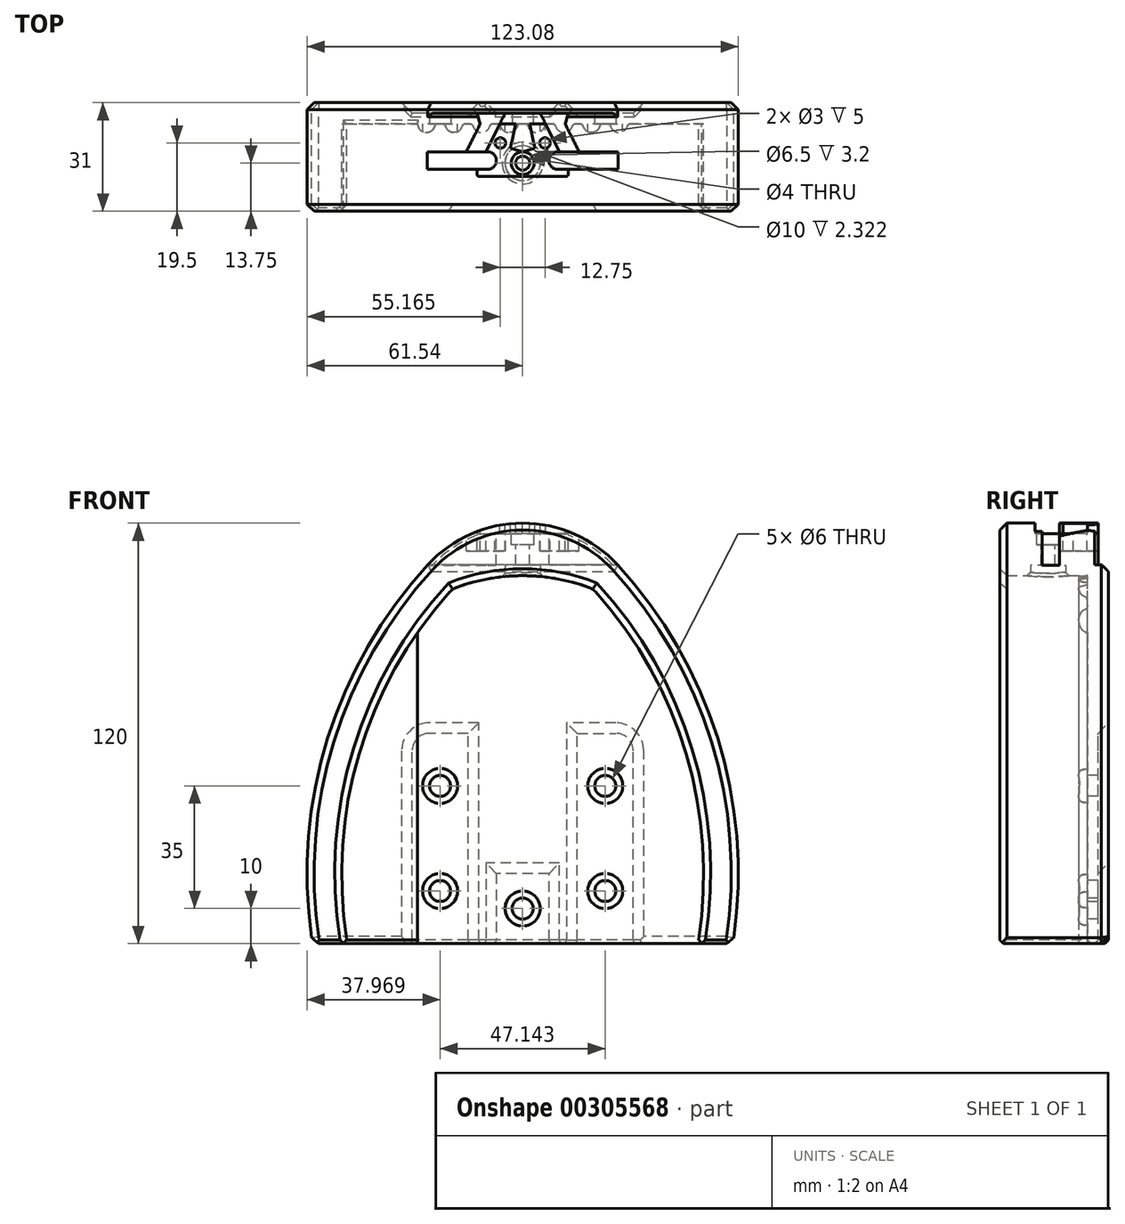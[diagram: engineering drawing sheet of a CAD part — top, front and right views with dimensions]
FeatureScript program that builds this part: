
annotation { "Feature Type Name" : "Feature", "Feature Type Description" : "" }
export const myFeature = defineFeature(function(context is Context, id is Id, definition is map)
    precondition{}
    {
        {
            assignVariable(context, id + "F0", {"name" : "LHeel", "anyValue" : 120 * mm});
        }
        {
            assignVariable(context, id + "F1", {"name" : "THeel", "anyValue" : 15 * mm});
        }
        {
            var Q0;
            Q0=qCreatedBy(makeId("Front.planeOp"),FACE);
            var sketch = newSketch(context, id + "F2", { "sketchPlane" : qUnion([Q0])});
            skArc(sketch, "E0", {"start": v(0, 120) * mm, "mid": v(-14.77, 116.9) * mm, "end": v(-27.05, 108.16) * mm});
            skArc(sketch, "E1", {"start": v(-27.05, 108.16) * mm, "mid": v(-55.9, 57.85) * mm, "end": v(-60, 0) * mm});
            skLineSegment(sketch, "E2", {"start": v(-60, 0) * mm, "end": v(0, 0) * mm});
            skArc(sketch, "E3.MirrorCS", {"start": v(0, 120) * mm, "mid": v(14.77, 116.9) * mm, "end": v(27.05, 108.16) * mm});
            skArc(sketch, "E4.MirrorCS", {"start": v(27.05, 108.16) * mm, "mid": v(55.9, 57.85) * mm, "end": v(60, 0) * mm});
            skLineSegment(sketch, "E5.MirrorCS", {"start": v(60, 0) * mm, "end": v(0, 0) * mm});
            skSolve(sketch);
        }
        {
            var Q0;
            Q0=makeQuery(id+"F2.imprint","IMPRINT",FACE,{"disambiguationData":[TD([[makeQuery(id+"F2.imprint","IMPRINT",EDGE,{"derivedFrom":sQuery(id+"F2.wireOp",EDGE,"E0")}),1.0]])]});
            extrude(context, id + "F3", {"entities" : qUnion([Q0]), "depth" : 3 * mm});
        }
        {
            var Q0;
            Q0=makeQuery(id+"F3.opExtrude","CAP_FACE",FACE,{"disambiguationData":[OSD([sQuery(id+"F2.wireOp",EDGE,"E0"),sQuery(id+"F2.wireOp",EDGE,"E1"),sQuery(id+"F2.wireOp",EDGE,"E2"),sQuery(id+"F2.wireOp",EDGE,"E3.MirrorCS"),sQuery(id+"F2.wireOp",EDGE,"E4.MirrorCS"),sQuery(id+"F2.wireOp",EDGE,"E5.MirrorCS")])],"isStart":false});
            var sketch = newSketch(context, id + "F4", { "sketchPlane" : qUnion([Q0])});
            skArc(sketch, "E6", {"start": v(0, 120) * mm, "mid": v(-14.77, 116.9) * mm, "end": v(-27.05, 108.16) * mm});
            skArc(sketch, "E7", {"start": v(-27.05, 108.16) * mm, "mid": v(-55.9, 57.85) * mm, "end": v(-60, 0) * mm});
            skArc(sketch, "E8", {"start": v(-20.01, 101.23) * mm, "mid": v(-46.72, 54.09) * mm, "end": v(-50, 0) * mm});
            skLineSegment(sketch, "E9", {"start": v(-60, 0) * mm, "end": v(-50, 0) * mm});
            skArc(sketch, "E10.MirrorCS", {"start": v(20.01, 101.23) * mm, "mid": v(46.72, 54.09) * mm, "end": v(50, 0) * mm});
            skLineSegment(sketch, "E11.MirrorCS", {"start": v(60, 0) * mm, "end": v(50, 0) * mm});
            skArc(sketch, "E12.MirrorCS", {"start": v(27.05, 108.16) * mm, "mid": v(55.9, 57.85) * mm, "end": v(60, 0) * mm});
            skArc(sketch, "E13.MirrorCS", {"start": v(0, 120) * mm, "mid": v(14.77, 116.9) * mm, "end": v(27.05, 108.16) * mm});
            skArc(sketch, "E14", {"start": v(20.01, 101.23) * mm, "mid": v(0, 105) * mm, "end": v(-20.01, 101.23) * mm});
            skPoint(sketch, "E15", {"position": v(0, 105) * mm});
            skSolve(sketch);
        }
        {
            var Q0;
            Q0=qSketchRegion(id+"F4",true);
            extrude(context, id + "F5", {"entities" : qUnion([Q0]), "operationType" : NewBodyOperationType.ADD, "depth" : 25 * mm});
        }
        {
            var Q0;
            Q0=makeQuery(id+"F3.opExtrude","SWEPT_FACE",FACE,{"disambiguationData":[OSD([sQuery(id+"F2.wireOp",EDGE,"E2"),sQuery(id+"F2.wireOp",EDGE,"E5.MirrorCS")])]});
            var sketch = newSketch(context, id + "F6", { "sketchPlane" : qUnion([Q0])});
            skArc(sketch, "E16", {"start": v(-25, 3) * mm, "mid": v(-27.5, 5.5) * mm, "end": v(-30, 3) * mm});
            skLineSegment(sketch, "E17", {"start": v(-30, 3) * mm, "end": v(-25, 3) * mm});
            skArc(sketch, "E18.1.0.0", {"start": v(-17.14, 3) * mm, "mid": v(-19.64, 5.5) * mm, "end": v(-22.14, 3) * mm});
            skArc(sketch, "E18.2.0.0", {"start": v(-9.29, 3) * mm, "mid": v(-11.79, 5.5) * mm, "end": v(-14.29, 3) * mm});
            skArc(sketch, "E18.3.0.0", {"start": v(-1.43, 3) * mm, "mid": v(-3.93, 5.5) * mm, "end": v(-6.43, 3) * mm});
            skArc(sketch, "E18.4.0.0", {"start": v(6.43, 3) * mm, "mid": v(3.93, 5.5) * mm, "end": v(1.43, 3) * mm});
            skArc(sketch, "E18.5.0.0", {"start": v(14.29, 3) * mm, "mid": v(11.79, 5.5) * mm, "end": v(9.29, 3) * mm});
            skArc(sketch, "E18.6.0.0", {"start": v(22.14, 3) * mm, "mid": v(19.64, 5.5) * mm, "end": v(17.14, 3) * mm});
            skArc(sketch, "E18.7.0.0", {"start": v(30, 3) * mm, "mid": v(27.5, 5.5) * mm, "end": v(25, 3) * mm});
            skLineSegment(sketch, "E18.direction1", {"start": v(-30, 3) * mm, "end": v(-22.14, 3) * mm, "construction": true});
            skSolve(sketch);
        }
        {
            var Q0;
            Q0=qSketchRegion(id+"F6",true);
            var Q1;
            {var subQ0=sQuery(id+"F6.wireOp",EDGE,"E18.1.0.0");Q1=makeQuery(id+"F6.imprint","IMPRINT",FACE,{"disambiguationData":[TD([[makeQuery(id+"F6.imprint","IMPRINT",EDGE,{"derivedFrom":subQ0}),1.0]])]});}
            var Q2;
            {var subQ0=sQuery(id+"F6.wireOp",EDGE,"E18.2.0.0");Q2=makeQuery(id+"F6.imprint","IMPRINT",FACE,{"disambiguationData":[TD([[makeQuery(id+"F6.imprint","IMPRINT",EDGE,{"derivedFrom":subQ0}),1.0]])]});}
            var Q3;
            {var subQ0=sQuery(id+"F6.wireOp",EDGE,"E18.3.0.0");Q3=makeQuery(id+"F6.imprint","IMPRINT",FACE,{"disambiguationData":[TD([[makeQuery(id+"F6.imprint","IMPRINT",EDGE,{"derivedFrom":subQ0}),1.0]])]});}
            var Q4;
            {var subQ0=sQuery(id+"F6.wireOp",EDGE,"E18.4.0.0");Q4=makeQuery(id+"F6.imprint","IMPRINT",FACE,{"disambiguationData":[TD([[makeQuery(id+"F6.imprint","IMPRINT",EDGE,{"derivedFrom":subQ0}),1.0]])]});}
            var Q5;
            {var subQ0=sQuery(id+"F6.wireOp",EDGE,"E18.5.0.0");Q5=makeQuery(id+"F6.imprint","IMPRINT",FACE,{"disambiguationData":[TD([[makeQuery(id+"F6.imprint","IMPRINT",EDGE,{"derivedFrom":subQ0}),1.0]])]});}
            var Q6;
            {var subQ0=sQuery(id+"F6.wireOp",EDGE,"E18.6.0.0");Q6=makeQuery(id+"F6.imprint","IMPRINT",FACE,{"disambiguationData":[TD([[makeQuery(id+"F6.imprint","IMPRINT",EDGE,{"derivedFrom":subQ0}),1.0]])]});}
            var Q7;
            {var subQ0=sQuery(id+"F6.wireOp",EDGE,"E18.7.0.0");Q7=makeQuery(id+"F6.imprint","IMPRINT",FACE,{"disambiguationData":[TD([[makeQuery(id+"F6.imprint","IMPRINT",EDGE,{"derivedFrom":subQ0}),1.0]])]});}
            var Q8;
            {var subQ0=sQuery(id+"F6.wireOp",EDGE,"E18.8.0.0");Q8=makeQuery(id+"F6.imprint","IMPRINT",FACE,{"disambiguationData":[TD([[makeQuery(id+"F6.imprint","IMPRINT",EDGE,{"derivedFrom":subQ0}),1.0]])]});}
            var Q9;
            {var subQ0=sQuery(id+"F6.wireOp",EDGE,"E18.9.0.0");Q9=makeQuery(id+"F6.imprint","IMPRINT",FACE,{"disambiguationData":[TD([[makeQuery(id+"F6.imprint","IMPRINT",EDGE,{"derivedFrom":subQ0}),1.0]])]});}
            extrude(context, id + "F7", {"entities" : qUnion([Q0, Q1, Q2, Q3, Q4, Q5, Q6, Q7, Q8, Q9]), "operationType" : NewBodyOperationType.ADD, "endBound" : BoundingType.UP_TO_NEXT, "oppositeDirection" : true, "depth" : 25 * mm});
        }
        {
            var Q0;
            {var subQ0=sQuery(id+"F6.wireOp",EDGE,"E17");var subQ1=sQuery(id+"F6.wireOp",EDGE,"E16");var subQ2=sQuery(id+"F2.wireOp",EDGE,"E5.MirrorCS");var subQ3=sQuery(id+"F2.wireOp",EDGE,"E2");Q0=makeQuery(id+"F7.opExtrude","SWEPT_EDGE",EDGE,{"disambiguationData":[OSD([subQ3,subQ2,subQ1,subQ0]),TDD([makeQuery(id+"F6.imprint","INTERSECT",VERTEX,{"disambiguationData":[OD(0.0)],"derivedFrom":[makeQuery(id+"F3.opExtrude","CAP_EDGE",EDGE,{"disambiguationData":[OSD([subQ3,subQ2])],"isStart":false}),subQ1,subQ0]})])]});}
            var Q1;
            {var subQ0=sQuery(id+"F6.wireOp",EDGE,"E18.1.0.0");var subQ1=sQuery(id+"F2.wireOp",EDGE,"E5.MirrorCS");var subQ2=sQuery(id+"F2.wireOp",EDGE,"E2");Q1=makeQuery(id+"F7.opExtrude","SWEPT_EDGE",EDGE,{"disambiguationData":[OSD([subQ2,subQ1,subQ0]),TDD([makeQuery(id+"F6.imprint","INTERSECT",VERTEX,{"disambiguationData":[OD(0.0)],"derivedFrom":[makeQuery(id+"F3.opExtrude","CAP_EDGE",EDGE,{"disambiguationData":[OSD([subQ2,subQ1])],"isStart":false}),subQ0]})])]});}
            var Q2;
            {var subQ0=sQuery(id+"F6.wireOp",EDGE,"E18.2.0.0");var subQ1=sQuery(id+"F2.wireOp",EDGE,"E5.MirrorCS");var subQ2=sQuery(id+"F2.wireOp",EDGE,"E2");Q2=makeQuery(id+"F7.opExtrude","SWEPT_EDGE",EDGE,{"disambiguationData":[OSD([subQ2,subQ1,subQ0]),TDD([makeQuery(id+"F6.imprint","INTERSECT",VERTEX,{"disambiguationData":[OD(0.0)],"derivedFrom":[makeQuery(id+"F3.opExtrude","CAP_EDGE",EDGE,{"disambiguationData":[OSD([subQ2,subQ1])],"isStart":false}),subQ0]})])]});}
            var Q3;
            {var subQ0=sQuery(id+"F6.wireOp",EDGE,"E18.3.0.0");var subQ1=sQuery(id+"F2.wireOp",EDGE,"E5.MirrorCS");var subQ2=sQuery(id+"F2.wireOp",EDGE,"E2");Q3=makeQuery(id+"F7.opExtrude","SWEPT_EDGE",EDGE,{"disambiguationData":[OSD([subQ2,subQ1,subQ0]),TDD([makeQuery(id+"F6.imprint","INTERSECT",VERTEX,{"disambiguationData":[OD(0.0)],"derivedFrom":[makeQuery(id+"F3.opExtrude","CAP_EDGE",EDGE,{"disambiguationData":[OSD([subQ2,subQ1])],"isStart":false}),subQ0]})])]});}
            var Q4;
            {var subQ0=sQuery(id+"F6.wireOp",EDGE,"E18.4.0.0");var subQ1=sQuery(id+"F2.wireOp",EDGE,"E5.MirrorCS");var subQ2=sQuery(id+"F2.wireOp",EDGE,"E2");Q4=makeQuery(id+"F7.opExtrude","SWEPT_EDGE",EDGE,{"disambiguationData":[OSD([subQ2,subQ1,subQ0]),TDD([makeQuery(id+"F6.imprint","INTERSECT",VERTEX,{"disambiguationData":[OD(0.0)],"derivedFrom":[makeQuery(id+"F3.opExtrude","CAP_EDGE",EDGE,{"disambiguationData":[OSD([subQ2,subQ1])],"isStart":false}),subQ0]})])]});}
            var Q5;
            {var subQ0=sQuery(id+"F6.wireOp",EDGE,"E18.5.0.0");var subQ1=sQuery(id+"F2.wireOp",EDGE,"E5.MirrorCS");var subQ2=sQuery(id+"F2.wireOp",EDGE,"E2");Q5=makeQuery(id+"F7.opExtrude","SWEPT_EDGE",EDGE,{"disambiguationData":[OSD([subQ2,subQ1,subQ0]),TDD([makeQuery(id+"F6.imprint","INTERSECT",VERTEX,{"disambiguationData":[OD(0.0)],"derivedFrom":[makeQuery(id+"F3.opExtrude","CAP_EDGE",EDGE,{"disambiguationData":[OSD([subQ2,subQ1])],"isStart":false}),subQ0]})])]});}
            var Q6;
            {var subQ0=sQuery(id+"F6.wireOp",EDGE,"E18.6.0.0");var subQ1=sQuery(id+"F2.wireOp",EDGE,"E5.MirrorCS");var subQ2=sQuery(id+"F2.wireOp",EDGE,"E2");Q6=makeQuery(id+"F7.opExtrude","SWEPT_EDGE",EDGE,{"disambiguationData":[OSD([subQ2,subQ1,subQ0]),TDD([makeQuery(id+"F6.imprint","INTERSECT",VERTEX,{"disambiguationData":[OD(0.0)],"derivedFrom":[makeQuery(id+"F3.opExtrude","CAP_EDGE",EDGE,{"disambiguationData":[OSD([subQ2,subQ1])],"isStart":false}),subQ0]})])]});}
            var Q7;
            {var subQ0=sQuery(id+"F6.wireOp",EDGE,"E18.7.0.0");var subQ1=sQuery(id+"F2.wireOp",EDGE,"E5.MirrorCS");var subQ2=sQuery(id+"F2.wireOp",EDGE,"E2");Q7=makeQuery(id+"F7.opExtrude","SWEPT_EDGE",EDGE,{"disambiguationData":[OSD([subQ2,subQ1,subQ0]),TDD([makeQuery(id+"F6.imprint","INTERSECT",VERTEX,{"disambiguationData":[OD(0.0)],"derivedFrom":[makeQuery(id+"F3.opExtrude","CAP_EDGE",EDGE,{"disambiguationData":[OSD([subQ2,subQ1])],"isStart":false}),subQ0]})])]});}
            var Q8;
            {var subQ0=sQuery(id+"F6.wireOp",EDGE,"E18.8.0.0");var subQ1=sQuery(id+"F2.wireOp",EDGE,"E5.MirrorCS");var subQ2=sQuery(id+"F2.wireOp",EDGE,"E2");Q8=makeQuery(id+"F7.opExtrude","SWEPT_EDGE",EDGE,{"disambiguationData":[OSD([subQ2,subQ1,subQ0]),TDD([makeQuery(id+"F6.imprint","INTERSECT",VERTEX,{"disambiguationData":[OD(0.0)],"derivedFrom":[makeQuery(id+"F3.opExtrude","CAP_EDGE",EDGE,{"disambiguationData":[OSD([subQ2,subQ1])],"isStart":false}),subQ0]})])]});}
            var Q9;
            {var subQ0=sQuery(id+"F6.wireOp",EDGE,"E18.9.0.0");var subQ1=sQuery(id+"F2.wireOp",EDGE,"E5.MirrorCS");var subQ2=sQuery(id+"F2.wireOp",EDGE,"E2");Q9=makeQuery(id+"F7.opExtrude","SWEPT_EDGE",EDGE,{"disambiguationData":[OSD([subQ2,subQ1,subQ0]),TDD([makeQuery(id+"F6.imprint","INTERSECT",VERTEX,{"disambiguationData":[OD(0.0)],"derivedFrom":[makeQuery(id+"F3.opExtrude","CAP_EDGE",EDGE,{"disambiguationData":[OSD([subQ2,subQ1])],"isStart":false}),subQ0]})])]});}
            var Q10;
            {var subQ0=sQuery(id+"F6.wireOp",EDGE,"E18.9.0.0");var subQ1=sQuery(id+"F2.wireOp",EDGE,"E5.MirrorCS");var subQ2=sQuery(id+"F2.wireOp",EDGE,"E2");Q10=makeQuery(id+"F7.opExtrude","SWEPT_EDGE",EDGE,{"disambiguationData":[OSD([subQ2,subQ1,subQ0]),TDD([makeQuery(id+"F6.imprint","INTERSECT",VERTEX,{"disambiguationData":[OD(1.0)],"derivedFrom":[makeQuery(id+"F3.opExtrude","CAP_EDGE",EDGE,{"disambiguationData":[OSD([subQ2,subQ1])],"isStart":false}),subQ0]})])]});}
            var Q11;
            {var subQ0=sQuery(id+"F6.wireOp",EDGE,"E18.8.0.0");var subQ1=sQuery(id+"F2.wireOp",EDGE,"E5.MirrorCS");var subQ2=sQuery(id+"F2.wireOp",EDGE,"E2");Q11=makeQuery(id+"F7.opExtrude","SWEPT_EDGE",EDGE,{"disambiguationData":[OSD([subQ2,subQ1,subQ0]),TDD([makeQuery(id+"F6.imprint","INTERSECT",VERTEX,{"disambiguationData":[OD(1.0)],"derivedFrom":[makeQuery(id+"F3.opExtrude","CAP_EDGE",EDGE,{"disambiguationData":[OSD([subQ2,subQ1])],"isStart":false}),subQ0]})])]});}
            var Q12;
            {var subQ0=sQuery(id+"F6.wireOp",EDGE,"E18.7.0.0");var subQ1=sQuery(id+"F2.wireOp",EDGE,"E5.MirrorCS");var subQ2=sQuery(id+"F2.wireOp",EDGE,"E2");Q12=makeQuery(id+"F7.opExtrude","SWEPT_EDGE",EDGE,{"disambiguationData":[OSD([subQ2,subQ1,subQ0]),TDD([makeQuery(id+"F6.imprint","INTERSECT",VERTEX,{"disambiguationData":[OD(1.0)],"derivedFrom":[makeQuery(id+"F3.opExtrude","CAP_EDGE",EDGE,{"disambiguationData":[OSD([subQ2,subQ1])],"isStart":false}),subQ0]})])]});}
            var Q13;
            {var subQ0=sQuery(id+"F6.wireOp",EDGE,"E18.6.0.0");var subQ1=sQuery(id+"F2.wireOp",EDGE,"E5.MirrorCS");var subQ2=sQuery(id+"F2.wireOp",EDGE,"E2");Q13=makeQuery(id+"F7.opExtrude","SWEPT_EDGE",EDGE,{"disambiguationData":[OSD([subQ2,subQ1,subQ0]),TDD([makeQuery(id+"F6.imprint","INTERSECT",VERTEX,{"disambiguationData":[OD(1.0)],"derivedFrom":[makeQuery(id+"F3.opExtrude","CAP_EDGE",EDGE,{"disambiguationData":[OSD([subQ2,subQ1])],"isStart":false}),subQ0]})])]});}
            var Q14;
            {var subQ0=sQuery(id+"F6.wireOp",EDGE,"E18.5.0.0");var subQ1=sQuery(id+"F2.wireOp",EDGE,"E5.MirrorCS");var subQ2=sQuery(id+"F2.wireOp",EDGE,"E2");Q14=makeQuery(id+"F7.opExtrude","SWEPT_EDGE",EDGE,{"disambiguationData":[OSD([subQ2,subQ1,subQ0]),TDD([makeQuery(id+"F6.imprint","INTERSECT",VERTEX,{"disambiguationData":[OD(1.0)],"derivedFrom":[makeQuery(id+"F3.opExtrude","CAP_EDGE",EDGE,{"disambiguationData":[OSD([subQ2,subQ1])],"isStart":false}),subQ0]})])]});}
            var Q15;
            {var subQ0=sQuery(id+"F6.wireOp",EDGE,"E18.4.0.0");var subQ1=sQuery(id+"F2.wireOp",EDGE,"E5.MirrorCS");var subQ2=sQuery(id+"F2.wireOp",EDGE,"E2");Q15=makeQuery(id+"F7.opExtrude","SWEPT_EDGE",EDGE,{"disambiguationData":[OSD([subQ2,subQ1,subQ0]),TDD([makeQuery(id+"F6.imprint","INTERSECT",VERTEX,{"disambiguationData":[OD(1.0)],"derivedFrom":[makeQuery(id+"F3.opExtrude","CAP_EDGE",EDGE,{"disambiguationData":[OSD([subQ2,subQ1])],"isStart":false}),subQ0]})])]});}
            var Q16;
            {var subQ0=sQuery(id+"F6.wireOp",EDGE,"E18.3.0.0");var subQ1=sQuery(id+"F2.wireOp",EDGE,"E5.MirrorCS");var subQ2=sQuery(id+"F2.wireOp",EDGE,"E2");Q16=makeQuery(id+"F7.opExtrude","SWEPT_EDGE",EDGE,{"disambiguationData":[OSD([subQ2,subQ1,subQ0]),TDD([makeQuery(id+"F6.imprint","INTERSECT",VERTEX,{"disambiguationData":[OD(1.0)],"derivedFrom":[makeQuery(id+"F3.opExtrude","CAP_EDGE",EDGE,{"disambiguationData":[OSD([subQ2,subQ1])],"isStart":false}),subQ0]})])]});}
            var Q17;
            {var subQ0=sQuery(id+"F6.wireOp",EDGE,"E18.2.0.0");var subQ1=sQuery(id+"F2.wireOp",EDGE,"E5.MirrorCS");var subQ2=sQuery(id+"F2.wireOp",EDGE,"E2");Q17=makeQuery(id+"F7.opExtrude","SWEPT_EDGE",EDGE,{"disambiguationData":[OSD([subQ2,subQ1,subQ0]),TDD([makeQuery(id+"F6.imprint","INTERSECT",VERTEX,{"disambiguationData":[OD(1.0)],"derivedFrom":[makeQuery(id+"F3.opExtrude","CAP_EDGE",EDGE,{"disambiguationData":[OSD([subQ2,subQ1])],"isStart":false}),subQ0]})])]});}
            var Q18;
            {var subQ0=sQuery(id+"F6.wireOp",EDGE,"E18.1.0.0");var subQ1=sQuery(id+"F2.wireOp",EDGE,"E5.MirrorCS");var subQ2=sQuery(id+"F2.wireOp",EDGE,"E2");Q18=makeQuery(id+"F7.opExtrude","SWEPT_EDGE",EDGE,{"disambiguationData":[OSD([subQ2,subQ1,subQ0]),TDD([makeQuery(id+"F6.imprint","INTERSECT",VERTEX,{"disambiguationData":[OD(1.0)],"derivedFrom":[makeQuery(id+"F3.opExtrude","CAP_EDGE",EDGE,{"disambiguationData":[OSD([subQ2,subQ1])],"isStart":false}),subQ0]})])]});}
            var Q19;
            {var subQ0=sQuery(id+"F6.wireOp",EDGE,"E17");var subQ1=sQuery(id+"F6.wireOp",EDGE,"E16");var subQ2=sQuery(id+"F2.wireOp",EDGE,"E5.MirrorCS");var subQ3=sQuery(id+"F2.wireOp",EDGE,"E2");Q19=makeQuery(id+"F7.opExtrude","SWEPT_EDGE",EDGE,{"disambiguationData":[OSD([subQ3,subQ2,subQ1,subQ0]),TDD([makeQuery(id+"F6.imprint","INTERSECT",VERTEX,{"disambiguationData":[OD(1.0)],"derivedFrom":[makeQuery(id+"F3.opExtrude","CAP_EDGE",EDGE,{"disambiguationData":[OSD([subQ3,subQ2])],"isStart":false}),subQ1,subQ0]})])]});}
            fillet(context, id + "F8", {"entities" : qUnion([Q0, Q1, Q2, Q3, Q4, Q5, Q6, Q7, Q8, Q9, Q10, Q11, Q12, Q13, Q14, Q15, Q16, Q17, Q18, Q19]), "radius" : 1 * mm, "tangentPropagation" : true, "allowEdgeOverflow" : false});
        }
        {
            var Q0;
            Q0=qCreatedBy(makeId("Top.planeOp"),FACE);
            cPlane(context, id + "F9", {"entities" : qUnion([Q0]), "cplaneType" : CPlaneType.OFFSET, "offset" : getVariable(context, 'LHeel'), "width" : 150 * mm, "height" : 150 * mm});
        }
        {
            var Q0;
            Q0=qCreatedBy(id+"F9.planeOp",FACE);
            var sketch = newSketch(context, id + "F10", { "sketchPlane" : qUnion([Q0])});
            skLineSegment(sketch, "E19", {"start": v(35, -11) * mm, "end": v(10, -11) * mm});
            skLineSegment(sketch, "E20", {"start": v(10, -16) * mm, "end": v(35, -16) * mm});
            skLineSegment(sketch, "E21", {"start": v(35, -16) * mm, "end": v(35, -11) * mm});
            skArc(sketch, "E22", {"start": v(10, -11) * mm, "mid": v(7.5, -13.5) * mm, "end": v(10, -16) * mm});
            skLineSegment(sketch, "E23.MirrorCS", {"start": v(-35, -11) * mm, "end": v(-10, -11) * mm});
            skLineSegment(sketch, "E24.MirrorCS", {"start": v(-35, -16) * mm, "end": v(-35, -11) * mm});
            skLineSegment(sketch, "E25.MirrorCS", {"start": v(-10, -16) * mm, "end": v(-35, -16) * mm});
            skArc(sketch, "E26.MirrorCS", {"start": v(-10, -11) * mm, "mid": v(-7.5, -13.5) * mm, "end": v(-10, -16) * mm});
            skSolve(sketch);
        }
        {
            var Q0;
            Q0=qSketchRegion(id+"F10",true);
            extrude(context, id + "F11", {"entities" : qUnion([Q0]), "operationType" : NewBodyOperationType.REMOVE, "oppositeDirection" : true, "depth" : 12 * mm});
        }
        {
            var Q0;
            Q0=qCreatedBy(id+"F9.planeOp",FACE);
            var sketch = newSketch(context, id + "F12", { "sketchPlane" : qUnion([Q0])});
            skLineSegment(sketch, "E27", {"start": v(-5, 0) * mm, "end": v(-10.5, -11) * mm});
            skLineSegment(sketch, "E28", {"start": v(-10.5, -11) * mm, "end": v(-16.1, -11) * mm});
            skLineSegment(sketch, "E29", {"start": v(-16.1, -11) * mm, "end": v(-12.16, -3.14) * mm});
            skLineSegment(sketch, "E30", {"start": v(-12.16, -3.14) * mm, "end": v(-13, 0) * mm});
            skLineSegment(sketch, "E31", {"start": v(-13, 0) * mm, "end": v(-5, 0) * mm});
            skLineSegment(sketch, "E32.MirrorCS", {"start": v(12.16, -3.14) * mm, "end": v(13, 0) * mm});
            skLineSegment(sketch, "E33.MirrorCS", {"start": v(13, 0) * mm, "end": v(5, 0) * mm});
            skLineSegment(sketch, "E34.MirrorCS", {"start": v(10.5, -11) * mm, "end": v(16.1, -11) * mm});
            skLineSegment(sketch, "E35.MirrorCS", {"start": v(16.1, -11) * mm, "end": v(12.16, -3.14) * mm});
            skLineSegment(sketch, "E36.MirrorCS", {"start": v(5, 0) * mm, "end": v(10.5, -11) * mm});
            skSolve(sketch);
        }
        {
            var Q0;
            Q0=qSketchRegion(id+"F12",true);
            extrude(context, id + "F13", {"entities" : qUnion([Q0]), "operationType" : NewBodyOperationType.REMOVE, "oppositeDirection" : true, "depth" : 8 * mm});
        }
        {
            var Q0;
            Q0=qCreatedBy(id+"F9.planeOp",FACE);
            var sketch = newSketch(context, id + "F14", { "sketchPlane" : qUnion([Q0])});
            skLineSegment(sketch, "E37", {"start": v(-6.5, -3) * mm, "end": v(-2, -3) * mm});
            skLineSegment(sketch, "E38", {"start": v(-2, -3) * mm, "end": v(-3.5, -10) * mm});
            skLineSegment(sketch, "E39", {"start": v(-3.5, -10) * mm, "end": v(0, -11) * mm});
            skLineSegment(sketch, "E40", {"start": v(-6.5, -3) * mm, "end": v(-10.5, -11) * mm});
            skLineSegment(sketch, "E41", {"start": v(-13, -16) * mm, "end": v(-13, -18) * mm});
            skLineSegment(sketch, "E42", {"start": v(-13, -18) * mm, "end": v(0, -18) * mm});
            skLineSegment(sketch, "E43", {"start": v(-13, -16) * mm, "end": v(-10, -16) * mm});
            skLineSegment(sketch, "E44.MirrorCS", {"start": v(6.5, -3) * mm, "end": v(2, -3) * mm});
            skLineSegment(sketch, "E45.MirrorCS", {"start": v(6.5, -3) * mm, "end": v(10.5, -11) * mm});
            skLineSegment(sketch, "E46.MirrorCS", {"start": v(3.5, -10) * mm, "end": v(0, -11) * mm});
            skLineSegment(sketch, "E47.MirrorCS", {"start": v(2, -3) * mm, "end": v(3.5, -10) * mm});
            skLineSegment(sketch, "E48.MirrorCS", {"start": v(13, -16) * mm, "end": v(13, -18) * mm});
            skLineSegment(sketch, "E49.MirrorCS", {"start": v(13, -18) * mm, "end": v(0, -18) * mm});
            skLineSegment(sketch, "E50.MirrorCS", {"start": v(13, -16) * mm, "end": v(10, -16) * mm});
            skLineSegment(sketch, "E51", {"start": v(-10.5, -11) * mm, "end": v(-10, -11) * mm});
            skArc(sketch, "E52", {"start": v(-10, -16) * mm, "mid": v(-7.5, -13.5) * mm, "end": v(-10, -11) * mm});
            skLineSegment(sketch, "E53.MirrorCS", {"start": v(10.5, -11) * mm, "end": v(10, -11) * mm});
            skArc(sketch, "E54.MirrorCS", {"start": v(10, -16) * mm, "mid": v(7.5, -13.5) * mm, "end": v(10, -11) * mm});
            skSolve(sketch);
        }
        {
            var Q0;
            Q0=qSketchRegion(id+"F14",true);
            extrude(context, id + "F15", {"entities" : qUnion([Q0]), "operationType" : NewBodyOperationType.REMOVE, "oppositeDirection" : true, "depth" : 3 * mm});
        }
        {
            var Q0;
            Q0=makeQuery(id+"F15.boolean.opBoolean","COPY",EDGE,{"derivedFrom":makeQuery(id+"F15.opExtrude","SWEPT_EDGE",EDGE,{"disambiguationData":[OSD([sQuery(id+"F14.wireOp",EDGE,"E48.MirrorCS"),sQuery(id+"F14.wireOp",EDGE,"E49.MirrorCS")])]})});
            var Q1;
            Q1=makeQuery(id+"F15.boolean.opBoolean","COPY",EDGE,{"derivedFrom":makeQuery(id+"F15.opExtrude","SWEPT_EDGE",EDGE,{"disambiguationData":[OSD([sQuery(id+"F14.wireOp",EDGE,"E41"),sQuery(id+"F14.wireOp",EDGE,"E42")])]})});
            fillet(context, id + "F16", {"entities" : qUnion([Q0, Q1]), "radius" : .5 * mm, "tangentPropagation" : true, "allowEdgeOverflow" : false});
        }
        {
            var Q0;
            Q0=makeQuery(id+"F15.boolean.opBoolean","COPY",FACE,{"derivedFrom":makeQuery(id+"F15.opExtrude","CAP_FACE",FACE,{"disambiguationData":[OSD([sQuery(id+"F14.wireOp",EDGE,"E37"),sQuery(id+"F14.wireOp",EDGE,"E38"),sQuery(id+"F14.wireOp",EDGE,"E39"),sQuery(id+"F14.wireOp",EDGE,"E40"),sQuery(id+"F14.wireOp",EDGE,"E41"),sQuery(id+"F14.wireOp",EDGE,"E42"),sQuery(id+"F14.wireOp",EDGE,"E43"),sQuery(id+"F14.wireOp",EDGE,"E44.MirrorCS"),sQuery(id+"F14.wireOp",EDGE,"E45.MirrorCS"),sQuery(id+"F14.wireOp",EDGE,"E46.MirrorCS"),sQuery(id+"F14.wireOp",EDGE,"E47.MirrorCS"),sQuery(id+"F14.wireOp",EDGE,"E48.MirrorCS"),sQuery(id+"F14.wireOp",EDGE,"E49.MirrorCS"),sQuery(id+"F14.wireOp",EDGE,"E50.MirrorCS"),sQuery(id+"F14.wireOp",EDGE,"E51"),sQuery(id+"F14.wireOp",EDGE,"E52"),sQuery(id+"F14.wireOp",EDGE,"E53.MirrorCS"),sQuery(id+"F14.wireOp",EDGE,"E54.MirrorCS")])],"isStart":false})});
            var sketch = newSketch(context, id + "F17", { "sketchPlane" : qUnion([Q0])});
            skCircle(sketch, "E55", {"center": v(0, -14.25) * mm, "radius": 3.25 * mm});
            skSolve(sketch);
        }
        {
            var Q0;
            Q0=qSketchRegion(id+"F17",true);
            extrude(context, id + "F18", {"entities" : qUnion([Q0]), "operationType" : NewBodyOperationType.REMOVE, "oppositeDirection" : true, "depth" : 3.2 * mm});
        }
        {
            var Q0;
            Q0=makeQuery(id+"F15.boolean.opBoolean","COPY",FACE,{"derivedFrom":makeQuery(id+"F15.opExtrude","CAP_FACE",FACE,{"disambiguationData":[OSD([sQuery(id+"F14.wireOp",EDGE,"E37"),sQuery(id+"F14.wireOp",EDGE,"E38"),sQuery(id+"F14.wireOp",EDGE,"E39"),sQuery(id+"F14.wireOp",EDGE,"E40"),sQuery(id+"F14.wireOp",EDGE,"E41"),sQuery(id+"F14.wireOp",EDGE,"E42"),sQuery(id+"F14.wireOp",EDGE,"E43"),sQuery(id+"F14.wireOp",EDGE,"E44.MirrorCS"),sQuery(id+"F14.wireOp",EDGE,"E45.MirrorCS"),sQuery(id+"F14.wireOp",EDGE,"E46.MirrorCS"),sQuery(id+"F14.wireOp",EDGE,"E47.MirrorCS"),sQuery(id+"F14.wireOp",EDGE,"E48.MirrorCS"),sQuery(id+"F14.wireOp",EDGE,"E49.MirrorCS"),sQuery(id+"F14.wireOp",EDGE,"E50.MirrorCS"),sQuery(id+"F14.wireOp",EDGE,"E51"),sQuery(id+"F14.wireOp",EDGE,"E52"),sQuery(id+"F14.wireOp",EDGE,"E53.MirrorCS"),sQuery(id+"F14.wireOp",EDGE,"E54.MirrorCS")])],"isStart":false})});
            var sketch = newSketch(context, id + "F19", { "sketchPlane" : qUnion([Q0])});
            skCircle(sketch, "E56", {"center": v(6.38, -8.5) * mm, "radius": 1.5 * mm});
            skCircle(sketch, "E57.MirrorC", {"center": v(-6.38, -8.5) * mm, "radius": 1.5 * mm});
            skSolve(sketch);
        }
        {
            var Q0;
            Q0=qSketchRegion(id+"F19",true);
            extrude(context, id + "F20", {"entities" : qUnion([Q0]), "operationType" : NewBodyOperationType.REMOVE, "oppositeDirection" : true, "depth" : 5 * mm});
        }
        {
            var Q0;
            Q0=makeQuery(id+"F15.boolean.opBoolean","COPY",FACE,{"derivedFrom":makeQuery(id+"F15.opExtrude","CAP_FACE",FACE,{"disambiguationData":[OSD([sQuery(id+"F14.wireOp",EDGE,"E37"),sQuery(id+"F14.wireOp",EDGE,"E38"),sQuery(id+"F14.wireOp",EDGE,"E39"),sQuery(id+"F14.wireOp",EDGE,"E40"),sQuery(id+"F14.wireOp",EDGE,"E41"),sQuery(id+"F14.wireOp",EDGE,"E42"),sQuery(id+"F14.wireOp",EDGE,"E43"),sQuery(id+"F14.wireOp",EDGE,"E44.MirrorCS"),sQuery(id+"F14.wireOp",EDGE,"E45.MirrorCS"),sQuery(id+"F14.wireOp",EDGE,"E46.MirrorCS"),sQuery(id+"F14.wireOp",EDGE,"E47.MirrorCS"),sQuery(id+"F14.wireOp",EDGE,"E48.MirrorCS"),sQuery(id+"F14.wireOp",EDGE,"E49.MirrorCS"),sQuery(id+"F14.wireOp",EDGE,"E50.MirrorCS"),sQuery(id+"F14.wireOp",EDGE,"E51"),sQuery(id+"F14.wireOp",EDGE,"E52"),sQuery(id+"F14.wireOp",EDGE,"E53.MirrorCS"),sQuery(id+"F14.wireOp",EDGE,"E54.MirrorCS")])],"isStart":false})});
            var sketch = newSketch(context, id + "F21", { "sketchPlane" : qUnion([Q0])});
            skCircle(sketch, "E58", {"center": v(0, -14.25) * mm, "radius": 2 * mm});
            skSolve(sketch);
        }
        {
            var Q0;
            Q0=qSketchRegion(id+"F21",true);
            extrude(context, id + "F22", {"entities" : qUnion([Q0]), "operationType" : NewBodyOperationType.REMOVE, "oppositeDirection" : true, "depth" : 25 * mm});
        }
        {
            var Q0;
            Q0=qCreatedBy(makeId("Top.planeOp"),FACE);
            cPlane(context, id + "F23", {"entities" : qUnion([Q0]), "cplaneType" : CPlaneType.OFFSET, "offset" : getVariable(context, 'LHeel') - getVariable(context, 'THeel'), "width" : 150 * mm, "height" : 150 * mm});
        }
        {
            var Q0;
            Q0=qCreatedBy(id+"F23.planeOp",FACE);
            var sketch = newSketch(context, id + "F24", { "sketchPlane" : qUnion([Q0])});
            skCircle(sketch, "E59", {"center": v(0, -14.25) * mm, "radius": 2 * mm});
            skCircle(sketch, "E60", {"center": v(0, -14.25) * mm, "radius": 5 * mm});
            skSolve(sketch);
        }
        {
            var Q0;
            Q0=qSketchRegion(id+"F24",true);
            extrude(context, id + "F25", {"entities" : qUnion([Q0]), "operationType" : NewBodyOperationType.REMOVE, "depth" : 3 * mm, "hasSecondDirection" : true, "secondDirectionOppositeDirection" : true, "secondDirectionDepth" : 25 * mm});
        }
        {
            var Q0;
            {var subQ0=sQuery(id+"F6.wireOp",EDGE,"E18.6.0.0");var subQ1=sQuery(id+"F2.wireOp",EDGE,"E5.MirrorCS");var subQ2=sQuery(id+"F2.wireOp",EDGE,"E2");var subQ3=makeQuery(id+"F7.opExtrude","CAP_FACE",FACE,{"disambiguationData":[OSD([subQ2,subQ1,subQ0])],"isStart":true});var subQ4=makeQuery(id+"F7.opExtrude","CAP_FACE",FACE,{"disambiguationData":[OSD([subQ2,subQ1,sQuery(id+"F6.wireOp",EDGE,"E18.4.0.0")])],"isStart":true});var subQ5=makeQuery(id+"F7.opExtrude","CAP_FACE",FACE,{"disambiguationData":[OSD([subQ2,subQ1,sQuery(id+"F6.wireOp",EDGE,"E18.3.0.0")])],"isStart":true});var subQ6=makeQuery(id+"F3.opExtrude","SWEPT_FACE",FACE,{"disambiguationData":[OSD([subQ2,subQ1])]});var subQ7=makeQuery(id+"F7.opExtrude","CAP_FACE",FACE,{"disambiguationData":[OSD([subQ2,subQ1,sQuery(id+"F6.wireOp",EDGE,"E18.2.0.0")])],"isStart":true});var subQ8=makeQuery(id+"F5.opExtrude","SWEPT_FACE",FACE,{"disambiguationData":[OSD([sQuery(id+"F4.wireOp",EDGE,"FZn0JHBI-A9Gq-jUhd-VDxp-ANsdCAXQZEyL"),sQuery(id+"F4.wireOp",EDGE,"94862bb9-d334-4f4f-86bf-2b5ff63ee9990.MirrorCS")])]});var subQ9=sQuery(id+"F6.wireOp",EDGE,"E18.7.0.0");var subQ10=makeQuery(id+"F7.opExtrude","SWEPT_FACE",FACE,{"disambiguationData":[OSD([subQ9])]});var subQ11=makeQuery(id+"F7.opExtrude","CAP_FACE",FACE,{"disambiguationData":[OSD([subQ2,subQ1,sQuery(id+"F6.wireOp",EDGE,"E18.1.0.0")])],"isStart":true});var subQ12=makeQuery(id+"F7.opExtrude","CAP_FACE",FACE,{"disambiguationData":[OSD([subQ2,subQ1,sQuery(id+"F6.wireOp",EDGE,"E18.5.0.0")])],"isStart":true});var subQ13=makeQuery(id+"F7.opExtrude","CAP_FACE",FACE,{"disambiguationData":[OSD([sQuery(id+"F6.wireOp",EDGE,"E16"),sQuery(id+"F6.wireOp",EDGE,"E17")])],"isStart":true});var subQ14=makeQuery(id+"F7.opExtrude","CAP_FACE",FACE,{"disambiguationData":[OSD([subQ2,subQ1,subQ9])],"isStart":true});var subQ15=sQuery(id+"F6.wireOp",EDGE,"E18.8.0.0");var subQ16=makeQuery(id+"F7.opExtrude","SWEPT_FACE",FACE,{"disambiguationData":[OSD([subQ15])]});var subQ17=makeQuery(id+"F7.opExtrude","CAP_FACE",FACE,{"disambiguationData":[OSD([subQ2,subQ1,subQ15])],"isStart":true});var subQ18=sQuery(id+"F6.wireOp",EDGE,"E18.9.0.0");var subQ19=makeQuery(id+"F7.opExtrude","CAP_FACE",FACE,{"disambiguationData":[OSD([subQ2,subQ1,subQ18])],"isStart":true});var subQ20=makeQuery(id+"F3.opExtrude","CAP_FACE",FACE,{"disambiguationData":[OSD([sQuery(id+"F2.wireOp",EDGE,"E0"),sQuery(id+"F2.wireOp",EDGE,"E1"),subQ2,sQuery(id+"F2.wireOp",EDGE,"E3.MirrorCS"),sQuery(id+"F2.wireOp",EDGE,"E4.MirrorCS"),subQ1])],"isStart":false});Q0=makeQuery(id+"FuolT4ABAihHTZn_1.boolean.opBoolean","MERGE",FACE,{"derivedFrom":[makeQuery(id+"F7.boolean.opBoolean","SPLIT",FACE,{"disambiguationData":[TD([subQ6,subQ8,makeQuery(id+"F5.opExtrude","SWEPT_FACE",FACE,{"disambiguationData":[OSD([sQuery(id+"F4.wireOp",EDGE,"E10.MirrorCS")])]}),subQ13,subQ11,subQ7,subQ5,subQ4,subQ12,subQ3,subQ14,subQ16,subQ17,makeQuery(id+"F7.opExtrude","SWEPT_FACE",FACE,{"disambiguationData":[OSD([subQ18])]}),subQ19])],"derivedFrom":subQ20}),makeQuery(id+"F7.boolean.opBoolean","SPLIT",FACE,{"disambiguationData":[TD([subQ6,subQ8,subQ13,subQ11,subQ7,subQ5,subQ4,subQ12,makeQuery(id+"F7.opExtrude","SWEPT_FACE",FACE,{"disambiguationData":[OSD([subQ0])]}),subQ3,subQ10,subQ14,subQ17,subQ19])],"derivedFrom":subQ20}),makeQuery(id+"F7.boolean.opBoolean","SPLIT",FACE,{"disambiguationData":[TD([subQ6,subQ8,subQ13,subQ11,subQ7,subQ5,subQ4,subQ12,subQ3,subQ10,subQ14,subQ16,subQ17,subQ19])],"derivedFrom":subQ20}),makeQuery(id+"FuolT4ABAihHTZn_1.opExtrude","SWEPT_FACE",FACE,{"disambiguationData":[OSD([sQuery(id+"FIxBE3dgotSAZQS_1.wireOp",EDGE,"DbaOr28i-rK8a-sUH4-Cgqk-jCIZV5dNe7y5.bottom")])]})]});}
            var sketch = newSketch(context, id + "F26", { "sketchPlane" : qUnion([Q0])});
            skCircle(sketch, "E61", {"center": v(-23.57, 45) * mm, "radius": 3 * mm});
            skCircle(sketch, "E62", {"center": v(-23.57, 15) * mm, "radius": 3 * mm});
            skCircle(sketch, "E63.MirrorC", {"center": v(23.57, 45) * mm, "radius": 3 * mm});
            skCircle(sketch, "E64.MirrorC", {"center": v(23.57, 15) * mm, "radius": 3 * mm});
            skPoint(sketch, "E65", {"position": v(-23.57, 0) * mm});
            skPoint(sketch, "E66", {"position": v(23.57, 0) * mm});
            skCircle(sketch, "E67", {"center": v(0, 10) * mm, "radius": 3 * mm});
            skPoint(sketch, "E68", {"position": v(0, 0) * mm});
            skSolve(sketch);
        }
        {
            var Q0;
            Q0=qSketchRegion(id+"F26",true);
            extrude(context, id + "F27", {"entities" : qUnion([Q0]), "operationType" : NewBodyOperationType.REMOVE, "oppositeDirection" : true, "depth" : 25 * mm});
        }
        {
            var Q0;
            {var subQ0=sQuery(id+"F2.wireOp",EDGE,"E5.MirrorCS");var subQ1=sQuery(id+"F2.wireOp",EDGE,"E2");var subQ2=sQuery(id+"F6.wireOp",EDGE,"E16");var subQ3=sQuery(id+"F2.wireOp",EDGE,"E1");Q0=makeQuery(id+"F7.boolean.opBoolean","SPLIT",FACE,{"disambiguationData":[TD([makeQuery(id+"F3.opExtrude","SWEPT_FACE",FACE,{"disambiguationData":[OSD([subQ3])]}),makeQuery(id+"F3.opExtrude","SWEPT_FACE",FACE,{"disambiguationData":[OSD([subQ1,subQ0])]}),makeQuery(id+"F5.opExtrude","SWEPT_FACE",FACE,{"disambiguationData":[OSD([sQuery(id+"F4.wireOp",EDGE,"E7")])]}),makeQuery(id+"F5.opExtrude","SWEPT_FACE",FACE,{"disambiguationData":[OSD([sQuery(id+"F4.wireOp",EDGE,"E8")])]}),makeQuery(id+"F5.opExtrude","SWEPT_FACE",FACE,{"disambiguationData":[OSD([sQuery(id+"F4.wireOp",EDGE,"E9")])]}),makeQuery(id+"F7.opExtrude","SWEPT_FACE",FACE,{"disambiguationData":[OSD([subQ2])]}),makeQuery(id+"F7.opExtrude","CAP_FACE",FACE,{"disambiguationData":[OSD([subQ2,sQuery(id+"F6.wireOp",EDGE,"E17")])],"isStart":true}),makeQuery(id+"F7.opExtrude","CAP_FACE",FACE,{"disambiguationData":[OSD([subQ1,subQ0,sQuery(id+"F6.wireOp",EDGE,"E18.1.0.0")])],"isStart":true}),makeQuery(id+"F7.opExtrude","CAP_FACE",FACE,{"disambiguationData":[OSD([subQ1,subQ0,sQuery(id+"F6.wireOp",EDGE,"E18.2.0.0")])],"isStart":true}),makeQuery(id+"F7.opExtrude","CAP_FACE",FACE,{"disambiguationData":[OSD([subQ1,subQ0,sQuery(id+"F6.wireOp",EDGE,"E18.3.0.0")])],"isStart":true}),makeQuery(id+"F7.opExtrude","CAP_FACE",FACE,{"disambiguationData":[OSD([subQ1,subQ0,sQuery(id+"F6.wireOp",EDGE,"E18.4.0.0")])],"isStart":true}),makeQuery(id+"F7.opExtrude","CAP_FACE",FACE,{"disambiguationData":[OSD([subQ1,subQ0,sQuery(id+"F6.wireOp",EDGE,"E18.5.0.0")])],"isStart":true}),makeQuery(id+"F7.opExtrude","CAP_FACE",FACE,{"disambiguationData":[OSD([subQ1,subQ0,sQuery(id+"F6.wireOp",EDGE,"E18.6.0.0")])],"isStart":true}),makeQuery(id+"F7.opExtrude","CAP_FACE",FACE,{"disambiguationData":[OSD([subQ1,subQ0,sQuery(id+"F6.wireOp",EDGE,"E18.7.0.0")])],"isStart":true}),makeQuery(id+"F7.opExtrude","CAP_FACE",FACE,{"disambiguationData":[OSD([subQ1,subQ0,sQuery(id+"F6.wireOp",EDGE,"E18.8.0.0")])],"isStart":true}),makeQuery(id+"F7.opExtrude","CAP_FACE",FACE,{"disambiguationData":[OSD([subQ1,subQ0,sQuery(id+"F6.wireOp",EDGE,"E18.9.0.0")])],"isStart":true})])],"derivedFrom":makeQuery(id+"F3.opExtrude","CAP_FACE",FACE,{"disambiguationData":[OSD([sQuery(id+"F2.wireOp",EDGE,"E0"),subQ3,subQ1,sQuery(id+"F2.wireOp",EDGE,"E3.MirrorCS"),sQuery(id+"F2.wireOp",EDGE,"E4.MirrorCS"),subQ0])],"isStart":false})});}
            var sketch = newSketch(context, id + "F28", { "sketchPlane" : qUnion([Q0])});
            skCircle(sketch, "E69", {"center": v(23.57, 45) * mm, "radius": 5 * mm});
            skCircle(sketch, "E70", {"center": v(-23.57, 45) * mm, "radius": 5 * mm});
            skCircle(sketch, "E71", {"center": v(-23.57, 15) * mm, "radius": 5 * mm});
            skCircle(sketch, "E72", {"center": v(23.57, 15) * mm, "radius": 5 * mm});
            skCircle(sketch, "E73", {"center": v(0, 10) * mm, "radius": 5 * mm});
            skSolve(sketch);
        }
        {
            var Q0;
            Q0=qSketchRegion(id+"F28",true);
            extrude(context, id + "F29", {"entities" : qUnion([Q0]), "operationType" : NewBodyOperationType.REMOVE, "depth" : 25 * mm});
        }
        {
            var Q0;
            Q0=makeQuery(id+"F3.opExtrude","CAP_FACE",FACE,{"disambiguationData":[OSD([sQuery(id+"F2.wireOp",EDGE,"E0"),sQuery(id+"F2.wireOp",EDGE,"E1"),sQuery(id+"F2.wireOp",EDGE,"E2"),sQuery(id+"F2.wireOp",EDGE,"E3.MirrorCS"),sQuery(id+"F2.wireOp",EDGE,"E4.MirrorCS"),sQuery(id+"F2.wireOp",EDGE,"E5.MirrorCS")])],"isStart":true});
            var sketch = newSketch(context, id + "F30", { "sketchPlane" : qUnion([Q0])});
            skArc(sketch, "E74", {"start": v(60, 0) * mm, "mid": v(55.9, 57.85) * mm, "end": v(27.05, 108.16) * mm});
            skPoint(sketch, "E75", {"position": v(-23.57, 15) * mm});
            skLineSegment(sketch, "E76", {"start": v(-31.57, 0) * mm, "end": v(-31.57, 90) * mm});
            skLineSegment(sketch, "E77", {"start": v(0, 90) * mm, "end": v(-31.57, 90) * mm});
            skArc(sketch, "E78.MirrorCS", {"start": v(-60, 0) * mm, "mid": v(-55.9, 57.85) * mm, "end": v(-27.05, 108.16) * mm});
            skPoint(sketch, "E79.MirrorP", {"position": v(23.57, 15) * mm});
            skLineSegment(sketch, "E80.MirrorCS", {"start": v(31.57, 0) * mm, "end": v(31.57, 90) * mm});
            skLineSegment(sketch, "E81.MirrorCS", {"start": v(0, 90) * mm, "end": v(31.57, 90) * mm});
            skLineSegment(sketch, "E82", {"start": v(-15.57, 0) * mm, "end": v(-15.57, 60) * mm});
            skLineSegment(sketch, "E83", {"start": v(-15.57, 60) * mm, "end": v(-31.57, 60) * mm});
            skPoint(sketch, "E84", {"position": v(-23.57, 45) * mm});
            skLineSegment(sketch, "E85.MirrorCS", {"start": v(15.57, 60) * mm, "end": v(31.57, 60) * mm});
            skLineSegment(sketch, "E86.MirrorCS", {"start": v(15.57, 0) * mm, "end": v(15.57, 60) * mm});
            skLineSegment(sketch, "E87", {"start": v(-27.05, 108.16) * mm, "end": v(27.05, 108.16) * mm});
            skLineSegment(sketch, "E88", {"start": v(-60, 0) * mm, "end": v(-31.57, 0) * mm});
            skLineSegment(sketch, "E89", {"start": v(31.57, 0) * mm, "end": v(60, 0) * mm});
            skLineSegment(sketch, "E90", {"start": v(-15.57, 0) * mm, "end": v(-7.5, 0) * mm});
            skLineSegment(sketch, "E91", {"start": v(-7.5, 0) * mm, "end": v(-7.5, 20) * mm});
            skLineSegment(sketch, "E92", {"start": v(-7.5, 20) * mm, "end": v(7.5, 20) * mm});
            skLineSegment(sketch, "E93", {"start": v(7.5, 20) * mm, "end": v(7.5, 0) * mm});
            skLineSegment(sketch, "E94", {"start": v(7.5, 0) * mm, "end": v(15.57, 0) * mm});
            skPoint(sketch, "E95", {"position": v(0, 20) * mm});
            skPoint(sketch, "E96", {"position": v(0, 0) * mm});
            skSolve(sketch);
        }
        {
            var Q0;
            Q0=qSketchRegion(id+"F30",true);
            extrude(context, id + "F31", {"entities" : qUnion([Q0]), "operationType" : NewBodyOperationType.ADD, "depth" : 3 * mm});
        }
        {
            var Q0;
            Q0=makeQuery(id+"F31.opExtrude","SWEPT_EDGE",EDGE,{"disambiguationData":[OSD([sQuery(id+"F30.wireOp",EDGE,"E76"),sQuery(id+"F30.wireOp",EDGE,"E77")])]});
            var Q1;
            Q1=makeQuery(id+"F31.opExtrude","SWEPT_EDGE",EDGE,{"disambiguationData":[OSD([sQuery(id+"F30.wireOp",EDGE,"E80.MirrorCS"),sQuery(id+"F30.wireOp",EDGE,"E81.MirrorCS")])]});
            fillet(context, id + "F32", {"entities" : qUnion([Q0, Q1]), "radius" : 5 * mm, "tangentPropagation" : true, "allowEdgeOverflow" : false});
        }
        {
            var Q0;
            Q0=makeQuery(id+"F31.opExtrude","CAP_EDGE",EDGE,{"disambiguationData":[OSD([sQuery(id+"F30.wireOp",EDGE,"E74")])],"isStart":false});
            var Q1;
            Q1=makeQuery(id+"F5.opExtrude","CAP_EDGE",EDGE,{"disambiguationData":[OSD([sQuery(id+"F4.wireOp",EDGE,"E7")])],"isStart":false});
            var Q2;
            Q2=makeQuery(id+"F5.opExtrude","CAP_EDGE",EDGE,{"disambiguationData":[OSD([sQuery(id+"F4.wireOp",EDGE,"E8")])],"isStart":false});
            var Q3;
            Q3=makeQuery(id+"F5.opExtrude","CAP_EDGE",EDGE,{"disambiguationData":[OSD([sQuery(id+"F4.wireOp",EDGE,"E14")])],"isStart":false});
            var Q4;
            Q4=makeQuery(id+"F5.opExtrude","CAP_EDGE",EDGE,{"disambiguationData":[OSD([sQuery(id+"F4.wireOp",EDGE,"E10.MirrorCS")])],"isStart":false});
            var Q5;
            Q5=makeQuery(id+"F31.opExtrude","CAP_EDGE",EDGE,{"disambiguationData":[OSD([sQuery(id+"F30.wireOp",EDGE,"E87")])],"isStart":false});
            var Q6;
            Q6=makeQuery(id+"F31.opExtrude","CAP_EDGE",EDGE,{"disambiguationData":[OSD([sQuery(id+"F30.wireOp",EDGE,"E78.MirrorCS")])],"isStart":false});
            var Q7;
            Q7=makeQuery(id+"F31.opExtrude","CAP_EDGE",EDGE,{"disambiguationData":[OSD([sQuery(id+"F30.wireOp",EDGE,"E89")])],"isStart":false});
            var Q8;
            Q8=makeQuery(id+"F31.opExtrude","CAP_EDGE",EDGE,{"disambiguationData":[OSD([sQuery(id+"F30.wireOp",EDGE,"SiEx8vhQ-fxaC-5RrE-m7GO-d7uEWHyiGlIe")])],"isStart":false});
            var Q9;
            Q9=makeQuery(id+"F31.opExtrude","CAP_EDGE",EDGE,{"disambiguationData":[OSD([sQuery(id+"F30.wireOp",EDGE,"E88")])],"isStart":false});
            var Q10;
            Q10=makeQuery(id+"F31.boolean.opBoolean","MERGE",EDGE,{"derivedFrom":[makeQuery(id+"F5.boolean.opBoolean","MERGE",EDGE,{"derivedFrom":[makeQuery(id+"F3.opExtrude","SWEPT_EDGE",EDGE,{"disambiguationData":[OSD([sQuery(id+"F2.wireOp",EDGE,"E4.MirrorCS"),sQuery(id+"F2.wireOp",EDGE,"E5.MirrorCS")])]}),makeQuery(id+"F5.opExtrude","SWEPT_EDGE",EDGE,{"disambiguationData":[OSD([sQuery(id+"F4.wireOp",EDGE,"E11.MirrorCS"),sQuery(id+"F4.wireOp",EDGE,"E12.MirrorCS")])]})]}),makeQuery(id+"F31.opExtrude","SWEPT_EDGE",EDGE,{"disambiguationData":[OSD([sQuery(id+"F30.wireOp",EDGE,"E78.MirrorCS"),sQuery(id+"F30.wireOp",EDGE,"E88")])]})]});
            var Q11;
            Q11=makeQuery(id+"F31.boolean.opBoolean","MERGE",EDGE,{"derivedFrom":[makeQuery(id+"F5.boolean.opBoolean","MERGE",EDGE,{"derivedFrom":[makeQuery(id+"F3.opExtrude","SWEPT_EDGE",EDGE,{"disambiguationData":[OSD([sQuery(id+"F2.wireOp",EDGE,"E1"),sQuery(id+"F2.wireOp",EDGE,"E2")])]}),makeQuery(id+"F5.opExtrude","SWEPT_EDGE",EDGE,{"disambiguationData":[OSD([sQuery(id+"F4.wireOp",EDGE,"E7"),sQuery(id+"F4.wireOp",EDGE,"E9")])]})]}),makeQuery(id+"F31.opExtrude","SWEPT_EDGE",EDGE,{"disambiguationData":[OSD([sQuery(id+"F30.wireOp",EDGE,"E74"),sQuery(id+"F30.wireOp",EDGE,"E89")])]})]});
            chamfer(context, id + "F33", {"entities" : qUnion([Q0, Q1, Q2, Q3, Q4, Q5, Q6, Q7, Q8, Q9, Q10, Q11]), "width" : 2 * mm, "tangentPropagation" : true});
        }
        {
            var Q0;
            Q0=makeQuery(id+"F31.opExtrude","CAP_EDGE",EDGE,{"disambiguationData":[OSD([sQuery(id+"F30.wireOp",EDGE,"E80.MirrorCS")])],"isStart":false});
            var Q1;
            Q1=makeQuery(id+"F31.opExtrude","CAP_EDGE",EDGE,{"disambiguationData":[OSD([sQuery(id+"F30.wireOp",EDGE,"E85.MirrorCS")])],"isStart":false});
            var Q2;
            Q2=makeQuery(id+"F31.opExtrude","CAP_EDGE",EDGE,{"disambiguationData":[OSD([sQuery(id+"F30.wireOp",EDGE,"E86.MirrorCS")])],"isStart":false});
            var Q3;
            Q3=makeQuery(id+"F31.opExtrude","CAP_EDGE",EDGE,{"disambiguationData":[OSD([sQuery(id+"F30.wireOp",EDGE,"E76")])],"isStart":false});
            var Q4;
            Q4=makeQuery(id+"F31.opExtrude","CAP_EDGE",EDGE,{"disambiguationData":[OSD([sQuery(id+"F30.wireOp",EDGE,"E83")])],"isStart":false});
            var Q5;
            Q5=makeQuery(id+"F31.opExtrude","CAP_EDGE",EDGE,{"disambiguationData":[OSD([sQuery(id+"F30.wireOp",EDGE,"E82")])],"isStart":false});
            var Q6;
            Q6=makeQuery(id+"F31.opExtrude","CAP_EDGE",EDGE,{"disambiguationData":[OSD([sQuery(id+"F30.wireOp",EDGE,"E78.MirrorCS")])],"isStart":false});
            var Q7;
            Q7=makeQuery(id+"F31.opExtrude","CAP_EDGE",EDGE,{"disambiguationData":[OSD([sQuery(id+"F30.wireOp",EDGE,"E74")])],"isStart":false});
            var Q8;
            Q8=makeQuery(id+"F31.opExtrude","CAP_EDGE",EDGE,{"disambiguationData":[OSD([sQuery(id+"F30.wireOp",EDGE,"E91")])],"isStart":false});
            var Q9;
            Q9=makeQuery(id+"F31.opExtrude","CAP_EDGE",EDGE,{"disambiguationData":[OSD([sQuery(id+"F30.wireOp",EDGE,"E92")])],"isStart":false});
            var Q10;
            Q10=makeQuery(id+"F31.opExtrude","CAP_EDGE",EDGE,{"disambiguationData":[OSD([sQuery(id+"F30.wireOp",EDGE,"E93")])],"isStart":false});
            chamfer(context, id + "F34", {"entities" : qUnion([Q0, Q1, Q2, Q3, Q4, Q5, Q6, Q7, Q8, Q9, Q10]), "width" : 3 * mm, "tangentPropagation" : true});
        }
        {
            var Q0;
            {var subQ0=sQuery(id+"F2.wireOp",EDGE,"E5.MirrorCS");var subQ1=sQuery(id+"F2.wireOp",EDGE,"E2");var subQ2=sQuery(id+"F6.wireOp",EDGE,"E16");Q0=makeQuery(id+"F7.boolean.opBoolean","SPLIT",EDGE,{"disambiguationData":[TD([makeQuery(id+"F3.opExtrude","CAP_FACE",FACE,{"disambiguationData":[OSD([sQuery(id+"F2.wireOp",EDGE,"E0"),sQuery(id+"F2.wireOp",EDGE,"E1"),subQ1,sQuery(id+"F2.wireOp",EDGE,"E3.MirrorCS"),sQuery(id+"F2.wireOp",EDGE,"E4.MirrorCS"),subQ0])],"isStart":false}),makeQuery(id+"F3.opExtrude","SWEPT_FACE",FACE,{"disambiguationData":[OSD([subQ1,subQ0])]}),makeQuery(id+"F5.opExtrude","SWEPT_FACE",FACE,{"disambiguationData":[OSD([sQuery(id+"F4.wireOp",EDGE,"E8")])]}),makeQuery(id+"F5.opExtrude","SWEPT_FACE",FACE,{"disambiguationData":[OSD([sQuery(id+"F4.wireOp",EDGE,"E9")])]}),makeQuery(id+"F5.opExtrude","SWEPT_FACE",FACE,{"disambiguationData":[OSD([sQuery(id+"F4.wireOp",EDGE,"E11.MirrorCS")])]}),makeQuery(id+"F7.opExtrude","SWEPT_FACE",FACE,{"disambiguationData":[OSD([subQ2])]}),makeQuery(id+"F7.opExtrude","CAP_FACE",FACE,{"disambiguationData":[OSD([subQ2,sQuery(id+"F6.wireOp",EDGE,"E17")])],"isStart":true}),makeQuery(id+"F7.opExtrude","CAP_FACE",FACE,{"disambiguationData":[OSD([subQ1,subQ0,sQuery(id+"F6.wireOp",EDGE,"E18.1.0.0")])],"isStart":true}),makeQuery(id+"F7.opExtrude","CAP_FACE",FACE,{"disambiguationData":[OSD([subQ1,subQ0,sQuery(id+"F6.wireOp",EDGE,"E18.2.0.0")])],"isStart":true}),makeQuery(id+"F7.opExtrude","CAP_FACE",FACE,{"disambiguationData":[OSD([subQ1,subQ0,sQuery(id+"F6.wireOp",EDGE,"E18.3.0.0")])],"isStart":true}),makeQuery(id+"F7.opExtrude","CAP_FACE",FACE,{"disambiguationData":[OSD([subQ1,subQ0,sQuery(id+"F6.wireOp",EDGE,"E18.4.0.0")])],"isStart":true}),makeQuery(id+"F7.opExtrude","CAP_FACE",FACE,{"disambiguationData":[OSD([subQ1,subQ0,sQuery(id+"F6.wireOp",EDGE,"E18.5.0.0")])],"isStart":true}),makeQuery(id+"F7.opExtrude","CAP_FACE",FACE,{"disambiguationData":[OSD([subQ1,subQ0,sQuery(id+"F6.wireOp",EDGE,"E18.6.0.0")])],"isStart":true}),makeQuery(id+"F7.opExtrude","CAP_FACE",FACE,{"disambiguationData":[OSD([subQ1,subQ0,sQuery(id+"F6.wireOp",EDGE,"E18.7.0.0")])],"isStart":true}),makeQuery(id+"F7.opExtrude","CAP_FACE",FACE,{"disambiguationData":[OSD([subQ1,subQ0,sQuery(id+"F6.wireOp",EDGE,"E18.8.0.0")])],"isStart":true}),makeQuery(id+"F7.opExtrude","CAP_FACE",FACE,{"disambiguationData":[OSD([subQ1,subQ0,sQuery(id+"F6.wireOp",EDGE,"E18.9.0.0")])],"isStart":true})])],"derivedFrom":makeQuery(id+"F3.opExtrude","CAP_EDGE",EDGE,{"disambiguationData":[OSD([subQ1,subQ0])],"isStart":false})});}
            chamfer(context, id + "F35", {"entities" : qUnion([Q0]), "width" : 1 * mm, "tangentPropagation" : true});
        }
        {
            var Q0;
            Q0=makeQuery(id+"F31.opExtrude","CAP_EDGE",EDGE,{"disambiguationData":[OSD([sQuery(id+"F30.wireOp",EDGE,"LmbyR1he-35kO-f53Q-696j-YAIKVnODTwI9")])],"isStart":false});
            var Q1;
            {var subQ0=sQuery(id+"F2.wireOp",EDGE,"E5.MirrorCS");var subQ1=sQuery(id+"F2.wireOp",EDGE,"E2");Q1=makeQuery(id+"F34.opChamfer","BLEND_EDGE",EDGE,{"blendedFrom":[makeQuery(id+"F31.opExtrude","CAP_EDGE",EDGE,{"disambiguationData":[OSD([sQuery(id+"F30.wireOp",EDGE,"E82")])],"isStart":false}),makeQuery(id+"F31.boolean.opBoolean","MERGE",FACE,{"derivedFrom":[makeQuery(id+"F7.boolean.opBoolean","MERGE",FACE,{"derivedFrom":[makeQuery(id+"F5.boolean.opBoolean","MERGE",FACE,{"derivedFrom":[makeQuery(id+"F3.opExtrude","SWEPT_FACE",FACE,{"disambiguationData":[OSD([subQ1,subQ0])]}),makeQuery(id+"F5.opExtrude","SWEPT_FACE",FACE,{"disambiguationData":[OSD([sQuery(id+"F4.wireOp",EDGE,"E9")])]}),makeQuery(id+"F5.opExtrude","SWEPT_FACE",FACE,{"disambiguationData":[OSD([sQuery(id+"F4.wireOp",EDGE,"E11.MirrorCS")])]})]}),makeQuery(id+"F7.opExtrude","CAP_FACE",FACE,{"disambiguationData":[OSD([sQuery(id+"F6.wireOp",EDGE,"E16"),sQuery(id+"F6.wireOp",EDGE,"E17")])],"isStart":true}),makeQuery(id+"F7.opExtrude","CAP_FACE",FACE,{"disambiguationData":[OSD([subQ1,subQ0,sQuery(id+"F6.wireOp",EDGE,"E18.1.0.0")])],"isStart":true}),makeQuery(id+"F7.opExtrude","CAP_FACE",FACE,{"disambiguationData":[OSD([subQ1,subQ0,sQuery(id+"F6.wireOp",EDGE,"E18.2.0.0")])],"isStart":true}),makeQuery(id+"F7.opExtrude","CAP_FACE",FACE,{"disambiguationData":[OSD([subQ1,subQ0,sQuery(id+"F6.wireOp",EDGE,"E18.3.0.0")])],"isStart":true}),makeQuery(id+"F7.opExtrude","CAP_FACE",FACE,{"disambiguationData":[OSD([subQ1,subQ0,sQuery(id+"F6.wireOp",EDGE,"E18.4.0.0")])],"isStart":true}),makeQuery(id+"F7.opExtrude","CAP_FACE",FACE,{"disambiguationData":[OSD([subQ1,subQ0,sQuery(id+"F6.wireOp",EDGE,"E18.5.0.0")])],"isStart":true}),makeQuery(id+"F7.opExtrude","CAP_FACE",FACE,{"disambiguationData":[OSD([subQ1,subQ0,sQuery(id+"F6.wireOp",EDGE,"E18.6.0.0")])],"isStart":true}),makeQuery(id+"F7.opExtrude","CAP_FACE",FACE,{"disambiguationData":[OSD([subQ1,subQ0,sQuery(id+"F6.wireOp",EDGE,"E18.7.0.0")])],"isStart":true}),makeQuery(id+"F7.opExtrude","CAP_FACE",FACE,{"disambiguationData":[OSD([subQ1,subQ0,sQuery(id+"F6.wireOp",EDGE,"E18.8.0.0")])],"isStart":true}),makeQuery(id+"F7.opExtrude","CAP_FACE",FACE,{"disambiguationData":[OSD([subQ1,subQ0,sQuery(id+"F6.wireOp",EDGE,"E18.9.0.0")])],"isStart":true})]}),makeQuery(id+"F31.opExtrude","SWEPT_FACE",FACE,{"disambiguationData":[OSD([sQuery(id+"F30.wireOp",EDGE,"LmbyR1he-35kO-f53Q-696j-YAIKVnODTwI9")])]}),makeQuery(id+"F31.opExtrude","SWEPT_FACE",FACE,{"disambiguationData":[OSD([sQuery(id+"F30.wireOp",EDGE,"lc0urJVt-xGFD-1UqV-AUzd-Ddt8hkDyLtwQ"),sQuery(id+"F30.wireOp",EDGE,"9e28845e-500e-4894-8802-eb7ad12137a13.MirrorCS")])]}),makeQuery(id+"F31.opExtrude","SWEPT_FACE",FACE,{"disambiguationData":[OSD([sQuery(id+"F30.wireOp",EDGE,"9e28845e-500e-4894-8802-eb7ad12137a10.MirrorCS")])]})]})],"blendedInto":[makeQuery(id+"F31.boolean.opBoolean","MERGE",FACE,{"derivedFrom":[makeQuery(id+"F7.boolean.opBoolean","MERGE",FACE,{"derivedFrom":[makeQuery(id+"F5.boolean.opBoolean","MERGE",FACE,{"derivedFrom":[makeQuery(id+"F3.opExtrude","SWEPT_FACE",FACE,{"disambiguationData":[OSD([subQ1,subQ0])]}),makeQuery(id+"F5.opExtrude","SWEPT_FACE",FACE,{"disambiguationData":[OSD([sQuery(id+"F4.wireOp",EDGE,"E9")])]}),makeQuery(id+"F5.opExtrude","SWEPT_FACE",FACE,{"disambiguationData":[OSD([sQuery(id+"F4.wireOp",EDGE,"E11.MirrorCS")])]})]}),makeQuery(id+"F7.opExtrude","CAP_FACE",FACE,{"disambiguationData":[OSD([sQuery(id+"F6.wireOp",EDGE,"E16"),sQuery(id+"F6.wireOp",EDGE,"E17")])],"isStart":true}),makeQuery(id+"F7.opExtrude","CAP_FACE",FACE,{"disambiguationData":[OSD([subQ1,subQ0,sQuery(id+"F6.wireOp",EDGE,"E18.1.0.0")])],"isStart":true}),makeQuery(id+"F7.opExtrude","CAP_FACE",FACE,{"disambiguationData":[OSD([subQ1,subQ0,sQuery(id+"F6.wireOp",EDGE,"E18.2.0.0")])],"isStart":true}),makeQuery(id+"F7.opExtrude","CAP_FACE",FACE,{"disambiguationData":[OSD([subQ1,subQ0,sQuery(id+"F6.wireOp",EDGE,"E18.3.0.0")])],"isStart":true}),makeQuery(id+"F7.opExtrude","CAP_FACE",FACE,{"disambiguationData":[OSD([subQ1,subQ0,sQuery(id+"F6.wireOp",EDGE,"E18.4.0.0")])],"isStart":true}),makeQuery(id+"F7.opExtrude","CAP_FACE",FACE,{"disambiguationData":[OSD([subQ1,subQ0,sQuery(id+"F6.wireOp",EDGE,"E18.5.0.0")])],"isStart":true}),makeQuery(id+"F7.opExtrude","CAP_FACE",FACE,{"disambiguationData":[OSD([subQ1,subQ0,sQuery(id+"F6.wireOp",EDGE,"E18.6.0.0")])],"isStart":true}),makeQuery(id+"F7.opExtrude","CAP_FACE",FACE,{"disambiguationData":[OSD([subQ1,subQ0,sQuery(id+"F6.wireOp",EDGE,"E18.7.0.0")])],"isStart":true}),makeQuery(id+"F7.opExtrude","CAP_FACE",FACE,{"disambiguationData":[OSD([subQ1,subQ0,sQuery(id+"F6.wireOp",EDGE,"E18.8.0.0")])],"isStart":true}),makeQuery(id+"F7.opExtrude","CAP_FACE",FACE,{"disambiguationData":[OSD([subQ1,subQ0,sQuery(id+"F6.wireOp",EDGE,"E18.9.0.0")])],"isStart":true})]}),makeQuery(id+"F31.opExtrude","SWEPT_FACE",FACE,{"disambiguationData":[OSD([sQuery(id+"F30.wireOp",EDGE,"LmbyR1he-35kO-f53Q-696j-YAIKVnODTwI9")])]}),makeQuery(id+"F31.opExtrude","SWEPT_FACE",FACE,{"disambiguationData":[OSD([sQuery(id+"F30.wireOp",EDGE,"lc0urJVt-xGFD-1UqV-AUzd-Ddt8hkDyLtwQ"),sQuery(id+"F30.wireOp",EDGE,"9e28845e-500e-4894-8802-eb7ad12137a13.MirrorCS")])]}),makeQuery(id+"F31.opExtrude","SWEPT_FACE",FACE,{"disambiguationData":[OSD([sQuery(id+"F30.wireOp",EDGE,"9e28845e-500e-4894-8802-eb7ad12137a10.MirrorCS")])]})]})]});}
            var Q2;
            {var subQ0=sQuery(id+"F2.wireOp",EDGE,"E5.MirrorCS");var subQ1=sQuery(id+"F2.wireOp",EDGE,"E2");Q2=makeQuery(id+"F31.boolean.opBoolean","SPLIT",EDGE,{"disambiguationData":[TD([makeQuery(id+"F31.opExtrude","SWEPT_FACE",FACE,{"disambiguationData":[OSD([sQuery(id+"F30.wireOp",EDGE,"E76")])]})])],"derivedFrom":makeQuery(id+"F3.opExtrude","CAP_EDGE",EDGE,{"disambiguationData":[OSD([subQ1,subQ0])],"isStart":true})});}
            var Q3;
            {var subQ0=sQuery(id+"F2.wireOp",EDGE,"E5.MirrorCS");var subQ1=sQuery(id+"F2.wireOp",EDGE,"E2");Q3=makeQuery(id+"F34.opChamfer","BLEND_EDGE",EDGE,{"blendedFrom":[makeQuery(id+"F31.opExtrude","CAP_EDGE",EDGE,{"disambiguationData":[OSD([sQuery(id+"F30.wireOp",EDGE,"E76")])],"isStart":false}),makeQuery(id+"F31.boolean.opBoolean","MERGE",FACE,{"derivedFrom":[makeQuery(id+"F7.boolean.opBoolean","MERGE",FACE,{"derivedFrom":[makeQuery(id+"F5.boolean.opBoolean","MERGE",FACE,{"derivedFrom":[makeQuery(id+"F3.opExtrude","SWEPT_FACE",FACE,{"disambiguationData":[OSD([subQ1,subQ0])]}),makeQuery(id+"F5.opExtrude","SWEPT_FACE",FACE,{"disambiguationData":[OSD([sQuery(id+"F4.wireOp",EDGE,"E9")])]}),makeQuery(id+"F5.opExtrude","SWEPT_FACE",FACE,{"disambiguationData":[OSD([sQuery(id+"F4.wireOp",EDGE,"E11.MirrorCS")])]})]}),makeQuery(id+"F7.opExtrude","CAP_FACE",FACE,{"disambiguationData":[OSD([sQuery(id+"F6.wireOp",EDGE,"E16"),sQuery(id+"F6.wireOp",EDGE,"E17")])],"isStart":true}),makeQuery(id+"F7.opExtrude","CAP_FACE",FACE,{"disambiguationData":[OSD([subQ1,subQ0,sQuery(id+"F6.wireOp",EDGE,"E18.1.0.0")])],"isStart":true}),makeQuery(id+"F7.opExtrude","CAP_FACE",FACE,{"disambiguationData":[OSD([subQ1,subQ0,sQuery(id+"F6.wireOp",EDGE,"E18.2.0.0")])],"isStart":true}),makeQuery(id+"F7.opExtrude","CAP_FACE",FACE,{"disambiguationData":[OSD([subQ1,subQ0,sQuery(id+"F6.wireOp",EDGE,"E18.3.0.0")])],"isStart":true}),makeQuery(id+"F7.opExtrude","CAP_FACE",FACE,{"disambiguationData":[OSD([subQ1,subQ0,sQuery(id+"F6.wireOp",EDGE,"E18.4.0.0")])],"isStart":true}),makeQuery(id+"F7.opExtrude","CAP_FACE",FACE,{"disambiguationData":[OSD([subQ1,subQ0,sQuery(id+"F6.wireOp",EDGE,"E18.5.0.0")])],"isStart":true}),makeQuery(id+"F7.opExtrude","CAP_FACE",FACE,{"disambiguationData":[OSD([subQ1,subQ0,sQuery(id+"F6.wireOp",EDGE,"E18.6.0.0")])],"isStart":true}),makeQuery(id+"F7.opExtrude","CAP_FACE",FACE,{"disambiguationData":[OSD([subQ1,subQ0,sQuery(id+"F6.wireOp",EDGE,"E18.7.0.0")])],"isStart":true}),makeQuery(id+"F7.opExtrude","CAP_FACE",FACE,{"disambiguationData":[OSD([subQ1,subQ0,sQuery(id+"F6.wireOp",EDGE,"E18.8.0.0")])],"isStart":true}),makeQuery(id+"F7.opExtrude","CAP_FACE",FACE,{"disambiguationData":[OSD([subQ1,subQ0,sQuery(id+"F6.wireOp",EDGE,"E18.9.0.0")])],"isStart":true})]}),makeQuery(id+"F31.opExtrude","SWEPT_FACE",FACE,{"disambiguationData":[OSD([sQuery(id+"F30.wireOp",EDGE,"LmbyR1he-35kO-f53Q-696j-YAIKVnODTwI9")])]}),makeQuery(id+"F31.opExtrude","SWEPT_FACE",FACE,{"disambiguationData":[OSD([sQuery(id+"F30.wireOp",EDGE,"lc0urJVt-xGFD-1UqV-AUzd-Ddt8hkDyLtwQ"),sQuery(id+"F30.wireOp",EDGE,"9e28845e-500e-4894-8802-eb7ad12137a13.MirrorCS")])]}),makeQuery(id+"F31.opExtrude","SWEPT_FACE",FACE,{"disambiguationData":[OSD([sQuery(id+"F30.wireOp",EDGE,"9e28845e-500e-4894-8802-eb7ad12137a10.MirrorCS")])]})]})],"blendedInto":[makeQuery(id+"F31.boolean.opBoolean","MERGE",FACE,{"derivedFrom":[makeQuery(id+"F7.boolean.opBoolean","MERGE",FACE,{"derivedFrom":[makeQuery(id+"F5.boolean.opBoolean","MERGE",FACE,{"derivedFrom":[makeQuery(id+"F3.opExtrude","SWEPT_FACE",FACE,{"disambiguationData":[OSD([subQ1,subQ0])]}),makeQuery(id+"F5.opExtrude","SWEPT_FACE",FACE,{"disambiguationData":[OSD([sQuery(id+"F4.wireOp",EDGE,"E9")])]}),makeQuery(id+"F5.opExtrude","SWEPT_FACE",FACE,{"disambiguationData":[OSD([sQuery(id+"F4.wireOp",EDGE,"E11.MirrorCS")])]})]}),makeQuery(id+"F7.opExtrude","CAP_FACE",FACE,{"disambiguationData":[OSD([sQuery(id+"F6.wireOp",EDGE,"E16"),sQuery(id+"F6.wireOp",EDGE,"E17")])],"isStart":true}),makeQuery(id+"F7.opExtrude","CAP_FACE",FACE,{"disambiguationData":[OSD([subQ1,subQ0,sQuery(id+"F6.wireOp",EDGE,"E18.1.0.0")])],"isStart":true}),makeQuery(id+"F7.opExtrude","CAP_FACE",FACE,{"disambiguationData":[OSD([subQ1,subQ0,sQuery(id+"F6.wireOp",EDGE,"E18.2.0.0")])],"isStart":true}),makeQuery(id+"F7.opExtrude","CAP_FACE",FACE,{"disambiguationData":[OSD([subQ1,subQ0,sQuery(id+"F6.wireOp",EDGE,"E18.3.0.0")])],"isStart":true}),makeQuery(id+"F7.opExtrude","CAP_FACE",FACE,{"disambiguationData":[OSD([subQ1,subQ0,sQuery(id+"F6.wireOp",EDGE,"E18.4.0.0")])],"isStart":true}),makeQuery(id+"F7.opExtrude","CAP_FACE",FACE,{"disambiguationData":[OSD([subQ1,subQ0,sQuery(id+"F6.wireOp",EDGE,"E18.5.0.0")])],"isStart":true}),makeQuery(id+"F7.opExtrude","CAP_FACE",FACE,{"disambiguationData":[OSD([subQ1,subQ0,sQuery(id+"F6.wireOp",EDGE,"E18.6.0.0")])],"isStart":true}),makeQuery(id+"F7.opExtrude","CAP_FACE",FACE,{"disambiguationData":[OSD([subQ1,subQ0,sQuery(id+"F6.wireOp",EDGE,"E18.7.0.0")])],"isStart":true}),makeQuery(id+"F7.opExtrude","CAP_FACE",FACE,{"disambiguationData":[OSD([subQ1,subQ0,sQuery(id+"F6.wireOp",EDGE,"E18.8.0.0")])],"isStart":true}),makeQuery(id+"F7.opExtrude","CAP_FACE",FACE,{"disambiguationData":[OSD([subQ1,subQ0,sQuery(id+"F6.wireOp",EDGE,"E18.9.0.0")])],"isStart":true})]}),makeQuery(id+"F31.opExtrude","SWEPT_FACE",FACE,{"disambiguationData":[OSD([sQuery(id+"F30.wireOp",EDGE,"LmbyR1he-35kO-f53Q-696j-YAIKVnODTwI9")])]}),makeQuery(id+"F31.opExtrude","SWEPT_FACE",FACE,{"disambiguationData":[OSD([sQuery(id+"F30.wireOp",EDGE,"lc0urJVt-xGFD-1UqV-AUzd-Ddt8hkDyLtwQ"),sQuery(id+"F30.wireOp",EDGE,"9e28845e-500e-4894-8802-eb7ad12137a13.MirrorCS")])]}),makeQuery(id+"F31.opExtrude","SWEPT_FACE",FACE,{"disambiguationData":[OSD([sQuery(id+"F30.wireOp",EDGE,"9e28845e-500e-4894-8802-eb7ad12137a10.MirrorCS")])]})]})]});}
            var Q4;
            Q4=makeQuery(id+"F31.opExtrude","CAP_EDGE",EDGE,{"disambiguationData":[OSD([sQuery(id+"F30.wireOp",EDGE,"lc0urJVt-xGFD-1UqV-AUzd-Ddt8hkDyLtwQ"),sQuery(id+"F30.wireOp",EDGE,"9e28845e-500e-4894-8802-eb7ad12137a13.MirrorCS")])],"isStart":false});
            var Q5;
            {var subQ0=sQuery(id+"F2.wireOp",EDGE,"E5.MirrorCS");var subQ1=sQuery(id+"F2.wireOp",EDGE,"E2");Q5=makeQuery(id+"F34.opChamfer","BLEND_EDGE",EDGE,{"blendedFrom":[makeQuery(id+"F31.opExtrude","CAP_EDGE",EDGE,{"disambiguationData":[OSD([sQuery(id+"F30.wireOp",EDGE,"E80.MirrorCS")])],"isStart":false}),makeQuery(id+"F31.boolean.opBoolean","MERGE",FACE,{"derivedFrom":[makeQuery(id+"F7.boolean.opBoolean","MERGE",FACE,{"derivedFrom":[makeQuery(id+"F5.boolean.opBoolean","MERGE",FACE,{"derivedFrom":[makeQuery(id+"F3.opExtrude","SWEPT_FACE",FACE,{"disambiguationData":[OSD([subQ1,subQ0])]}),makeQuery(id+"F5.opExtrude","SWEPT_FACE",FACE,{"disambiguationData":[OSD([sQuery(id+"F4.wireOp",EDGE,"E9")])]}),makeQuery(id+"F5.opExtrude","SWEPT_FACE",FACE,{"disambiguationData":[OSD([sQuery(id+"F4.wireOp",EDGE,"E11.MirrorCS")])]})]}),makeQuery(id+"F7.opExtrude","CAP_FACE",FACE,{"disambiguationData":[OSD([sQuery(id+"F6.wireOp",EDGE,"E16"),sQuery(id+"F6.wireOp",EDGE,"E17")])],"isStart":true}),makeQuery(id+"F7.opExtrude","CAP_FACE",FACE,{"disambiguationData":[OSD([subQ1,subQ0,sQuery(id+"F6.wireOp",EDGE,"E18.1.0.0")])],"isStart":true}),makeQuery(id+"F7.opExtrude","CAP_FACE",FACE,{"disambiguationData":[OSD([subQ1,subQ0,sQuery(id+"F6.wireOp",EDGE,"E18.2.0.0")])],"isStart":true}),makeQuery(id+"F7.opExtrude","CAP_FACE",FACE,{"disambiguationData":[OSD([subQ1,subQ0,sQuery(id+"F6.wireOp",EDGE,"E18.3.0.0")])],"isStart":true}),makeQuery(id+"F7.opExtrude","CAP_FACE",FACE,{"disambiguationData":[OSD([subQ1,subQ0,sQuery(id+"F6.wireOp",EDGE,"E18.4.0.0")])],"isStart":true}),makeQuery(id+"F7.opExtrude","CAP_FACE",FACE,{"disambiguationData":[OSD([subQ1,subQ0,sQuery(id+"F6.wireOp",EDGE,"E18.5.0.0")])],"isStart":true}),makeQuery(id+"F7.opExtrude","CAP_FACE",FACE,{"disambiguationData":[OSD([subQ1,subQ0,sQuery(id+"F6.wireOp",EDGE,"E18.6.0.0")])],"isStart":true}),makeQuery(id+"F7.opExtrude","CAP_FACE",FACE,{"disambiguationData":[OSD([subQ1,subQ0,sQuery(id+"F6.wireOp",EDGE,"E18.7.0.0")])],"isStart":true}),makeQuery(id+"F7.opExtrude","CAP_FACE",FACE,{"disambiguationData":[OSD([subQ1,subQ0,sQuery(id+"F6.wireOp",EDGE,"E18.8.0.0")])],"isStart":true}),makeQuery(id+"F7.opExtrude","CAP_FACE",FACE,{"disambiguationData":[OSD([subQ1,subQ0,sQuery(id+"F6.wireOp",EDGE,"E18.9.0.0")])],"isStart":true})]}),makeQuery(id+"F31.opExtrude","SWEPT_FACE",FACE,{"disambiguationData":[OSD([sQuery(id+"F30.wireOp",EDGE,"LmbyR1he-35kO-f53Q-696j-YAIKVnODTwI9")])]}),makeQuery(id+"F31.opExtrude","SWEPT_FACE",FACE,{"disambiguationData":[OSD([sQuery(id+"F30.wireOp",EDGE,"lc0urJVt-xGFD-1UqV-AUzd-Ddt8hkDyLtwQ"),sQuery(id+"F30.wireOp",EDGE,"9e28845e-500e-4894-8802-eb7ad12137a13.MirrorCS")])]}),makeQuery(id+"F31.opExtrude","SWEPT_FACE",FACE,{"disambiguationData":[OSD([sQuery(id+"F30.wireOp",EDGE,"9e28845e-500e-4894-8802-eb7ad12137a10.MirrorCS")])]})]})],"blendedInto":[makeQuery(id+"F31.boolean.opBoolean","MERGE",FACE,{"derivedFrom":[makeQuery(id+"F7.boolean.opBoolean","MERGE",FACE,{"derivedFrom":[makeQuery(id+"F5.boolean.opBoolean","MERGE",FACE,{"derivedFrom":[makeQuery(id+"F3.opExtrude","SWEPT_FACE",FACE,{"disambiguationData":[OSD([subQ1,subQ0])]}),makeQuery(id+"F5.opExtrude","SWEPT_FACE",FACE,{"disambiguationData":[OSD([sQuery(id+"F4.wireOp",EDGE,"E9")])]}),makeQuery(id+"F5.opExtrude","SWEPT_FACE",FACE,{"disambiguationData":[OSD([sQuery(id+"F4.wireOp",EDGE,"E11.MirrorCS")])]})]}),makeQuery(id+"F7.opExtrude","CAP_FACE",FACE,{"disambiguationData":[OSD([sQuery(id+"F6.wireOp",EDGE,"E16"),sQuery(id+"F6.wireOp",EDGE,"E17")])],"isStart":true}),makeQuery(id+"F7.opExtrude","CAP_FACE",FACE,{"disambiguationData":[OSD([subQ1,subQ0,sQuery(id+"F6.wireOp",EDGE,"E18.1.0.0")])],"isStart":true}),makeQuery(id+"F7.opExtrude","CAP_FACE",FACE,{"disambiguationData":[OSD([subQ1,subQ0,sQuery(id+"F6.wireOp",EDGE,"E18.2.0.0")])],"isStart":true}),makeQuery(id+"F7.opExtrude","CAP_FACE",FACE,{"disambiguationData":[OSD([subQ1,subQ0,sQuery(id+"F6.wireOp",EDGE,"E18.3.0.0")])],"isStart":true}),makeQuery(id+"F7.opExtrude","CAP_FACE",FACE,{"disambiguationData":[OSD([subQ1,subQ0,sQuery(id+"F6.wireOp",EDGE,"E18.4.0.0")])],"isStart":true}),makeQuery(id+"F7.opExtrude","CAP_FACE",FACE,{"disambiguationData":[OSD([subQ1,subQ0,sQuery(id+"F6.wireOp",EDGE,"E18.5.0.0")])],"isStart":true}),makeQuery(id+"F7.opExtrude","CAP_FACE",FACE,{"disambiguationData":[OSD([subQ1,subQ0,sQuery(id+"F6.wireOp",EDGE,"E18.6.0.0")])],"isStart":true}),makeQuery(id+"F7.opExtrude","CAP_FACE",FACE,{"disambiguationData":[OSD([subQ1,subQ0,sQuery(id+"F6.wireOp",EDGE,"E18.7.0.0")])],"isStart":true}),makeQuery(id+"F7.opExtrude","CAP_FACE",FACE,{"disambiguationData":[OSD([subQ1,subQ0,sQuery(id+"F6.wireOp",EDGE,"E18.8.0.0")])],"isStart":true}),makeQuery(id+"F7.opExtrude","CAP_FACE",FACE,{"disambiguationData":[OSD([subQ1,subQ0,sQuery(id+"F6.wireOp",EDGE,"E18.9.0.0")])],"isStart":true})]}),makeQuery(id+"F31.opExtrude","SWEPT_FACE",FACE,{"disambiguationData":[OSD([sQuery(id+"F30.wireOp",EDGE,"LmbyR1he-35kO-f53Q-696j-YAIKVnODTwI9")])]}),makeQuery(id+"F31.opExtrude","SWEPT_FACE",FACE,{"disambiguationData":[OSD([sQuery(id+"F30.wireOp",EDGE,"lc0urJVt-xGFD-1UqV-AUzd-Ddt8hkDyLtwQ"),sQuery(id+"F30.wireOp",EDGE,"9e28845e-500e-4894-8802-eb7ad12137a13.MirrorCS")])]}),makeQuery(id+"F31.opExtrude","SWEPT_FACE",FACE,{"disambiguationData":[OSD([sQuery(id+"F30.wireOp",EDGE,"9e28845e-500e-4894-8802-eb7ad12137a10.MirrorCS")])]})]})]});}
            var Q6;
            {var subQ0=sQuery(id+"F2.wireOp",EDGE,"E5.MirrorCS");var subQ1=sQuery(id+"F2.wireOp",EDGE,"E2");Q6=makeQuery(id+"F31.boolean.opBoolean","SPLIT",EDGE,{"disambiguationData":[TD([makeQuery(id+"F31.opExtrude","SWEPT_FACE",FACE,{"disambiguationData":[OSD([sQuery(id+"F30.wireOp",EDGE,"E80.MirrorCS")])]})])],"derivedFrom":makeQuery(id+"F3.opExtrude","CAP_EDGE",EDGE,{"disambiguationData":[OSD([subQ1,subQ0])],"isStart":true})});}
            var Q7;
            {var subQ0=sQuery(id+"F2.wireOp",EDGE,"E5.MirrorCS");var subQ1=sQuery(id+"F2.wireOp",EDGE,"E2");Q7=makeQuery(id+"F34.opChamfer","BLEND_EDGE",EDGE,{"blendedFrom":[makeQuery(id+"F31.opExtrude","CAP_EDGE",EDGE,{"disambiguationData":[OSD([sQuery(id+"F30.wireOp",EDGE,"E86.MirrorCS")])],"isStart":false}),makeQuery(id+"F31.boolean.opBoolean","MERGE",FACE,{"derivedFrom":[makeQuery(id+"F7.boolean.opBoolean","MERGE",FACE,{"derivedFrom":[makeQuery(id+"F5.boolean.opBoolean","MERGE",FACE,{"derivedFrom":[makeQuery(id+"F3.opExtrude","SWEPT_FACE",FACE,{"disambiguationData":[OSD([subQ1,subQ0])]}),makeQuery(id+"F5.opExtrude","SWEPT_FACE",FACE,{"disambiguationData":[OSD([sQuery(id+"F4.wireOp",EDGE,"E9")])]}),makeQuery(id+"F5.opExtrude","SWEPT_FACE",FACE,{"disambiguationData":[OSD([sQuery(id+"F4.wireOp",EDGE,"E11.MirrorCS")])]})]}),makeQuery(id+"F7.opExtrude","CAP_FACE",FACE,{"disambiguationData":[OSD([sQuery(id+"F6.wireOp",EDGE,"E16"),sQuery(id+"F6.wireOp",EDGE,"E17")])],"isStart":true}),makeQuery(id+"F7.opExtrude","CAP_FACE",FACE,{"disambiguationData":[OSD([subQ1,subQ0,sQuery(id+"F6.wireOp",EDGE,"E18.1.0.0")])],"isStart":true}),makeQuery(id+"F7.opExtrude","CAP_FACE",FACE,{"disambiguationData":[OSD([subQ1,subQ0,sQuery(id+"F6.wireOp",EDGE,"E18.2.0.0")])],"isStart":true}),makeQuery(id+"F7.opExtrude","CAP_FACE",FACE,{"disambiguationData":[OSD([subQ1,subQ0,sQuery(id+"F6.wireOp",EDGE,"E18.3.0.0")])],"isStart":true}),makeQuery(id+"F7.opExtrude","CAP_FACE",FACE,{"disambiguationData":[OSD([subQ1,subQ0,sQuery(id+"F6.wireOp",EDGE,"E18.4.0.0")])],"isStart":true}),makeQuery(id+"F7.opExtrude","CAP_FACE",FACE,{"disambiguationData":[OSD([subQ1,subQ0,sQuery(id+"F6.wireOp",EDGE,"E18.5.0.0")])],"isStart":true}),makeQuery(id+"F7.opExtrude","CAP_FACE",FACE,{"disambiguationData":[OSD([subQ1,subQ0,sQuery(id+"F6.wireOp",EDGE,"E18.6.0.0")])],"isStart":true}),makeQuery(id+"F7.opExtrude","CAP_FACE",FACE,{"disambiguationData":[OSD([subQ1,subQ0,sQuery(id+"F6.wireOp",EDGE,"E18.7.0.0")])],"isStart":true}),makeQuery(id+"F7.opExtrude","CAP_FACE",FACE,{"disambiguationData":[OSD([subQ1,subQ0,sQuery(id+"F6.wireOp",EDGE,"E18.8.0.0")])],"isStart":true}),makeQuery(id+"F7.opExtrude","CAP_FACE",FACE,{"disambiguationData":[OSD([subQ1,subQ0,sQuery(id+"F6.wireOp",EDGE,"E18.9.0.0")])],"isStart":true})]}),makeQuery(id+"F31.opExtrude","SWEPT_FACE",FACE,{"disambiguationData":[OSD([sQuery(id+"F30.wireOp",EDGE,"LmbyR1he-35kO-f53Q-696j-YAIKVnODTwI9")])]}),makeQuery(id+"F31.opExtrude","SWEPT_FACE",FACE,{"disambiguationData":[OSD([sQuery(id+"F30.wireOp",EDGE,"lc0urJVt-xGFD-1UqV-AUzd-Ddt8hkDyLtwQ"),sQuery(id+"F30.wireOp",EDGE,"9e28845e-500e-4894-8802-eb7ad12137a13.MirrorCS")])]}),makeQuery(id+"F31.opExtrude","SWEPT_FACE",FACE,{"disambiguationData":[OSD([sQuery(id+"F30.wireOp",EDGE,"9e28845e-500e-4894-8802-eb7ad12137a10.MirrorCS")])]})]})],"blendedInto":[makeQuery(id+"F31.boolean.opBoolean","MERGE",FACE,{"derivedFrom":[makeQuery(id+"F7.boolean.opBoolean","MERGE",FACE,{"derivedFrom":[makeQuery(id+"F5.boolean.opBoolean","MERGE",FACE,{"derivedFrom":[makeQuery(id+"F3.opExtrude","SWEPT_FACE",FACE,{"disambiguationData":[OSD([subQ1,subQ0])]}),makeQuery(id+"F5.opExtrude","SWEPT_FACE",FACE,{"disambiguationData":[OSD([sQuery(id+"F4.wireOp",EDGE,"E9")])]}),makeQuery(id+"F5.opExtrude","SWEPT_FACE",FACE,{"disambiguationData":[OSD([sQuery(id+"F4.wireOp",EDGE,"E11.MirrorCS")])]})]}),makeQuery(id+"F7.opExtrude","CAP_FACE",FACE,{"disambiguationData":[OSD([sQuery(id+"F6.wireOp",EDGE,"E16"),sQuery(id+"F6.wireOp",EDGE,"E17")])],"isStart":true}),makeQuery(id+"F7.opExtrude","CAP_FACE",FACE,{"disambiguationData":[OSD([subQ1,subQ0,sQuery(id+"F6.wireOp",EDGE,"E18.1.0.0")])],"isStart":true}),makeQuery(id+"F7.opExtrude","CAP_FACE",FACE,{"disambiguationData":[OSD([subQ1,subQ0,sQuery(id+"F6.wireOp",EDGE,"E18.2.0.0")])],"isStart":true}),makeQuery(id+"F7.opExtrude","CAP_FACE",FACE,{"disambiguationData":[OSD([subQ1,subQ0,sQuery(id+"F6.wireOp",EDGE,"E18.3.0.0")])],"isStart":true}),makeQuery(id+"F7.opExtrude","CAP_FACE",FACE,{"disambiguationData":[OSD([subQ1,subQ0,sQuery(id+"F6.wireOp",EDGE,"E18.4.0.0")])],"isStart":true}),makeQuery(id+"F7.opExtrude","CAP_FACE",FACE,{"disambiguationData":[OSD([subQ1,subQ0,sQuery(id+"F6.wireOp",EDGE,"E18.5.0.0")])],"isStart":true}),makeQuery(id+"F7.opExtrude","CAP_FACE",FACE,{"disambiguationData":[OSD([subQ1,subQ0,sQuery(id+"F6.wireOp",EDGE,"E18.6.0.0")])],"isStart":true}),makeQuery(id+"F7.opExtrude","CAP_FACE",FACE,{"disambiguationData":[OSD([subQ1,subQ0,sQuery(id+"F6.wireOp",EDGE,"E18.7.0.0")])],"isStart":true}),makeQuery(id+"F7.opExtrude","CAP_FACE",FACE,{"disambiguationData":[OSD([subQ1,subQ0,sQuery(id+"F6.wireOp",EDGE,"E18.8.0.0")])],"isStart":true}),makeQuery(id+"F7.opExtrude","CAP_FACE",FACE,{"disambiguationData":[OSD([subQ1,subQ0,sQuery(id+"F6.wireOp",EDGE,"E18.9.0.0")])],"isStart":true})]}),makeQuery(id+"F31.opExtrude","SWEPT_FACE",FACE,{"disambiguationData":[OSD([sQuery(id+"F30.wireOp",EDGE,"LmbyR1he-35kO-f53Q-696j-YAIKVnODTwI9")])]}),makeQuery(id+"F31.opExtrude","SWEPT_FACE",FACE,{"disambiguationData":[OSD([sQuery(id+"F30.wireOp",EDGE,"lc0urJVt-xGFD-1UqV-AUzd-Ddt8hkDyLtwQ"),sQuery(id+"F30.wireOp",EDGE,"9e28845e-500e-4894-8802-eb7ad12137a13.MirrorCS")])]}),makeQuery(id+"F31.opExtrude","SWEPT_FACE",FACE,{"disambiguationData":[OSD([sQuery(id+"F30.wireOp",EDGE,"9e28845e-500e-4894-8802-eb7ad12137a10.MirrorCS")])]})]})]});}
            var Q8;
            Q8=makeQuery(id+"F31.opExtrude","CAP_EDGE",EDGE,{"disambiguationData":[OSD([sQuery(id+"F30.wireOp",EDGE,"9e28845e-500e-4894-8802-eb7ad12137a10.MirrorCS")])],"isStart":false});
            var Q9;
            {var subQ0=sQuery(id+"F2.wireOp",EDGE,"E5.MirrorCS");var subQ1=sQuery(id+"F2.wireOp",EDGE,"E2");Q9=makeQuery(id+"F34.opChamfer","BLEND_EDGE",EDGE,{"blendedFrom":[makeQuery(id+"F31.opExtrude","CAP_EDGE",EDGE,{"disambiguationData":[OSD([sQuery(id+"F30.wireOp",EDGE,"E74")])],"isStart":false}),makeQuery(id+"F31.boolean.opBoolean","MERGE",FACE,{"derivedFrom":[makeQuery(id+"F7.boolean.opBoolean","MERGE",FACE,{"derivedFrom":[makeQuery(id+"F5.boolean.opBoolean","MERGE",FACE,{"derivedFrom":[makeQuery(id+"F3.opExtrude","SWEPT_FACE",FACE,{"disambiguationData":[OSD([subQ1,subQ0])]}),makeQuery(id+"F5.opExtrude","SWEPT_FACE",FACE,{"disambiguationData":[OSD([sQuery(id+"F4.wireOp",EDGE,"E9")])]}),makeQuery(id+"F5.opExtrude","SWEPT_FACE",FACE,{"disambiguationData":[OSD([sQuery(id+"F4.wireOp",EDGE,"E11.MirrorCS")])]})]}),makeQuery(id+"F7.opExtrude","CAP_FACE",FACE,{"disambiguationData":[OSD([sQuery(id+"F6.wireOp",EDGE,"E16"),sQuery(id+"F6.wireOp",EDGE,"E17")])],"isStart":true}),makeQuery(id+"F7.opExtrude","CAP_FACE",FACE,{"disambiguationData":[OSD([subQ1,subQ0,sQuery(id+"F6.wireOp",EDGE,"E18.1.0.0")])],"isStart":true}),makeQuery(id+"F7.opExtrude","CAP_FACE",FACE,{"disambiguationData":[OSD([subQ1,subQ0,sQuery(id+"F6.wireOp",EDGE,"E18.2.0.0")])],"isStart":true}),makeQuery(id+"F7.opExtrude","CAP_FACE",FACE,{"disambiguationData":[OSD([subQ1,subQ0,sQuery(id+"F6.wireOp",EDGE,"E18.3.0.0")])],"isStart":true}),makeQuery(id+"F7.opExtrude","CAP_FACE",FACE,{"disambiguationData":[OSD([subQ1,subQ0,sQuery(id+"F6.wireOp",EDGE,"E18.4.0.0")])],"isStart":true}),makeQuery(id+"F7.opExtrude","CAP_FACE",FACE,{"disambiguationData":[OSD([subQ1,subQ0,sQuery(id+"F6.wireOp",EDGE,"E18.5.0.0")])],"isStart":true}),makeQuery(id+"F7.opExtrude","CAP_FACE",FACE,{"disambiguationData":[OSD([subQ1,subQ0,sQuery(id+"F6.wireOp",EDGE,"E18.6.0.0")])],"isStart":true}),makeQuery(id+"F7.opExtrude","CAP_FACE",FACE,{"disambiguationData":[OSD([subQ1,subQ0,sQuery(id+"F6.wireOp",EDGE,"E18.7.0.0")])],"isStart":true}),makeQuery(id+"F7.opExtrude","CAP_FACE",FACE,{"disambiguationData":[OSD([subQ1,subQ0,sQuery(id+"F6.wireOp",EDGE,"E18.8.0.0")])],"isStart":true}),makeQuery(id+"F7.opExtrude","CAP_FACE",FACE,{"disambiguationData":[OSD([subQ1,subQ0,sQuery(id+"F6.wireOp",EDGE,"E18.9.0.0")])],"isStart":true})]}),makeQuery(id+"F31.opExtrude","SWEPT_FACE",FACE,{"disambiguationData":[OSD([sQuery(id+"F30.wireOp",EDGE,"LmbyR1he-35kO-f53Q-696j-YAIKVnODTwI9")])]}),makeQuery(id+"F31.opExtrude","SWEPT_FACE",FACE,{"disambiguationData":[OSD([sQuery(id+"F30.wireOp",EDGE,"lc0urJVt-xGFD-1UqV-AUzd-Ddt8hkDyLtwQ"),sQuery(id+"F30.wireOp",EDGE,"9e28845e-500e-4894-8802-eb7ad12137a13.MirrorCS")])]}),makeQuery(id+"F31.opExtrude","SWEPT_FACE",FACE,{"disambiguationData":[OSD([sQuery(id+"F30.wireOp",EDGE,"9e28845e-500e-4894-8802-eb7ad12137a10.MirrorCS")])]})]})],"blendedInto":[makeQuery(id+"F31.boolean.opBoolean","MERGE",FACE,{"derivedFrom":[makeQuery(id+"F7.boolean.opBoolean","MERGE",FACE,{"derivedFrom":[makeQuery(id+"F5.boolean.opBoolean","MERGE",FACE,{"derivedFrom":[makeQuery(id+"F3.opExtrude","SWEPT_FACE",FACE,{"disambiguationData":[OSD([subQ1,subQ0])]}),makeQuery(id+"F5.opExtrude","SWEPT_FACE",FACE,{"disambiguationData":[OSD([sQuery(id+"F4.wireOp",EDGE,"E9")])]}),makeQuery(id+"F5.opExtrude","SWEPT_FACE",FACE,{"disambiguationData":[OSD([sQuery(id+"F4.wireOp",EDGE,"E11.MirrorCS")])]})]}),makeQuery(id+"F7.opExtrude","CAP_FACE",FACE,{"disambiguationData":[OSD([sQuery(id+"F6.wireOp",EDGE,"E16"),sQuery(id+"F6.wireOp",EDGE,"E17")])],"isStart":true}),makeQuery(id+"F7.opExtrude","CAP_FACE",FACE,{"disambiguationData":[OSD([subQ1,subQ0,sQuery(id+"F6.wireOp",EDGE,"E18.1.0.0")])],"isStart":true}),makeQuery(id+"F7.opExtrude","CAP_FACE",FACE,{"disambiguationData":[OSD([subQ1,subQ0,sQuery(id+"F6.wireOp",EDGE,"E18.2.0.0")])],"isStart":true}),makeQuery(id+"F7.opExtrude","CAP_FACE",FACE,{"disambiguationData":[OSD([subQ1,subQ0,sQuery(id+"F6.wireOp",EDGE,"E18.3.0.0")])],"isStart":true}),makeQuery(id+"F7.opExtrude","CAP_FACE",FACE,{"disambiguationData":[OSD([subQ1,subQ0,sQuery(id+"F6.wireOp",EDGE,"E18.4.0.0")])],"isStart":true}),makeQuery(id+"F7.opExtrude","CAP_FACE",FACE,{"disambiguationData":[OSD([subQ1,subQ0,sQuery(id+"F6.wireOp",EDGE,"E18.5.0.0")])],"isStart":true}),makeQuery(id+"F7.opExtrude","CAP_FACE",FACE,{"disambiguationData":[OSD([subQ1,subQ0,sQuery(id+"F6.wireOp",EDGE,"E18.6.0.0")])],"isStart":true}),makeQuery(id+"F7.opExtrude","CAP_FACE",FACE,{"disambiguationData":[OSD([subQ1,subQ0,sQuery(id+"F6.wireOp",EDGE,"E18.7.0.0")])],"isStart":true}),makeQuery(id+"F7.opExtrude","CAP_FACE",FACE,{"disambiguationData":[OSD([subQ1,subQ0,sQuery(id+"F6.wireOp",EDGE,"E18.8.0.0")])],"isStart":true}),makeQuery(id+"F7.opExtrude","CAP_FACE",FACE,{"disambiguationData":[OSD([subQ1,subQ0,sQuery(id+"F6.wireOp",EDGE,"E18.9.0.0")])],"isStart":true})]}),makeQuery(id+"F31.opExtrude","SWEPT_FACE",FACE,{"disambiguationData":[OSD([sQuery(id+"F30.wireOp",EDGE,"LmbyR1he-35kO-f53Q-696j-YAIKVnODTwI9")])]}),makeQuery(id+"F31.opExtrude","SWEPT_FACE",FACE,{"disambiguationData":[OSD([sQuery(id+"F30.wireOp",EDGE,"lc0urJVt-xGFD-1UqV-AUzd-Ddt8hkDyLtwQ"),sQuery(id+"F30.wireOp",EDGE,"9e28845e-500e-4894-8802-eb7ad12137a13.MirrorCS")])]}),makeQuery(id+"F31.opExtrude","SWEPT_FACE",FACE,{"disambiguationData":[OSD([sQuery(id+"F30.wireOp",EDGE,"9e28845e-500e-4894-8802-eb7ad12137a10.MirrorCS")])]})]})]});}
            var Q10;
            Q10=makeQuery(id+"F31.boolean.opBoolean","MERGE",EDGE,{"derivedFrom":[makeQuery(id+"F5.boolean.opBoolean","MERGE",EDGE,{"derivedFrom":[makeQuery(id+"F3.opExtrude","SWEPT_EDGE",EDGE,{"disambiguationData":[OSD([sQuery(id+"F2.wireOp",EDGE,"E1"),sQuery(id+"F2.wireOp",EDGE,"E2")])]}),makeQuery(id+"F5.opExtrude","SWEPT_EDGE",EDGE,{"disambiguationData":[OSD([sQuery(id+"F4.wireOp",EDGE,"E7"),sQuery(id+"F4.wireOp",EDGE,"E9")])]})]}),makeQuery(id+"F31.opExtrude","SWEPT_EDGE",EDGE,{"disambiguationData":[OSD([sQuery(id+"F30.wireOp",EDGE,"E74"),sQuery(id+"F30.wireOp",EDGE,"LmbyR1he-35kO-f53Q-696j-YAIKVnODTwI9")])]})]});
            var Q11;
            Q11=makeQuery(id+"F5.opExtrude","CAP_EDGE",EDGE,{"disambiguationData":[OSD([sQuery(id+"F4.wireOp",EDGE,"E9")])],"isStart":false});
            var Q12;
            Q12=makeQuery(id+"F5.opExtrude","SWEPT_EDGE",EDGE,{"disambiguationData":[OSD([sQuery(id+"F2.wireOp",EDGE,"E2"),sQuery(id+"F2.wireOp",EDGE,"E5.MirrorCS"),sQuery(id+"F4.wireOp",EDGE,"E8"),sQuery(id+"F4.wireOp",EDGE,"E9")])]});
            var Q13;
            {var subQ0=sQuery(id+"F2.wireOp",EDGE,"E5.MirrorCS");var subQ1=sQuery(id+"F2.wireOp",EDGE,"E2");Q13=makeQuery(id+"F34.opChamfer","BLEND_EDGE",EDGE,{"blendedFrom":[makeQuery(id+"F31.opExtrude","CAP_EDGE",EDGE,{"disambiguationData":[OSD([sQuery(id+"F30.wireOp",EDGE,"E78.MirrorCS")])],"isStart":false}),makeQuery(id+"F31.boolean.opBoolean","MERGE",FACE,{"derivedFrom":[makeQuery(id+"F7.boolean.opBoolean","MERGE",FACE,{"derivedFrom":[makeQuery(id+"F5.boolean.opBoolean","MERGE",FACE,{"derivedFrom":[makeQuery(id+"F3.opExtrude","SWEPT_FACE",FACE,{"disambiguationData":[OSD([subQ1,subQ0])]}),makeQuery(id+"F5.opExtrude","SWEPT_FACE",FACE,{"disambiguationData":[OSD([sQuery(id+"F4.wireOp",EDGE,"E9")])]}),makeQuery(id+"F5.opExtrude","SWEPT_FACE",FACE,{"disambiguationData":[OSD([sQuery(id+"F4.wireOp",EDGE,"E11.MirrorCS")])]})]}),makeQuery(id+"F7.opExtrude","CAP_FACE",FACE,{"disambiguationData":[OSD([sQuery(id+"F6.wireOp",EDGE,"E16"),sQuery(id+"F6.wireOp",EDGE,"E17")])],"isStart":true}),makeQuery(id+"F7.opExtrude","CAP_FACE",FACE,{"disambiguationData":[OSD([subQ1,subQ0,sQuery(id+"F6.wireOp",EDGE,"E18.1.0.0")])],"isStart":true}),makeQuery(id+"F7.opExtrude","CAP_FACE",FACE,{"disambiguationData":[OSD([subQ1,subQ0,sQuery(id+"F6.wireOp",EDGE,"E18.2.0.0")])],"isStart":true}),makeQuery(id+"F7.opExtrude","CAP_FACE",FACE,{"disambiguationData":[OSD([subQ1,subQ0,sQuery(id+"F6.wireOp",EDGE,"E18.3.0.0")])],"isStart":true}),makeQuery(id+"F7.opExtrude","CAP_FACE",FACE,{"disambiguationData":[OSD([subQ1,subQ0,sQuery(id+"F6.wireOp",EDGE,"E18.4.0.0")])],"isStart":true}),makeQuery(id+"F7.opExtrude","CAP_FACE",FACE,{"disambiguationData":[OSD([subQ1,subQ0,sQuery(id+"F6.wireOp",EDGE,"E18.5.0.0")])],"isStart":true}),makeQuery(id+"F7.opExtrude","CAP_FACE",FACE,{"disambiguationData":[OSD([subQ1,subQ0,sQuery(id+"F6.wireOp",EDGE,"E18.6.0.0")])],"isStart":true}),makeQuery(id+"F7.opExtrude","CAP_FACE",FACE,{"disambiguationData":[OSD([subQ1,subQ0,sQuery(id+"F6.wireOp",EDGE,"E18.7.0.0")])],"isStart":true}),makeQuery(id+"F7.opExtrude","CAP_FACE",FACE,{"disambiguationData":[OSD([subQ1,subQ0,sQuery(id+"F6.wireOp",EDGE,"E18.8.0.0")])],"isStart":true}),makeQuery(id+"F7.opExtrude","CAP_FACE",FACE,{"disambiguationData":[OSD([subQ1,subQ0,sQuery(id+"F6.wireOp",EDGE,"E18.9.0.0")])],"isStart":true})]}),makeQuery(id+"F31.opExtrude","SWEPT_FACE",FACE,{"disambiguationData":[OSD([sQuery(id+"F30.wireOp",EDGE,"LmbyR1he-35kO-f53Q-696j-YAIKVnODTwI9")])]}),makeQuery(id+"F31.opExtrude","SWEPT_FACE",FACE,{"disambiguationData":[OSD([sQuery(id+"F30.wireOp",EDGE,"lc0urJVt-xGFD-1UqV-AUzd-Ddt8hkDyLtwQ"),sQuery(id+"F30.wireOp",EDGE,"9e28845e-500e-4894-8802-eb7ad12137a13.MirrorCS")])]}),makeQuery(id+"F31.opExtrude","SWEPT_FACE",FACE,{"disambiguationData":[OSD([sQuery(id+"F30.wireOp",EDGE,"9e28845e-500e-4894-8802-eb7ad12137a10.MirrorCS")])]})]})],"blendedInto":[makeQuery(id+"F31.boolean.opBoolean","MERGE",FACE,{"derivedFrom":[makeQuery(id+"F7.boolean.opBoolean","MERGE",FACE,{"derivedFrom":[makeQuery(id+"F5.boolean.opBoolean","MERGE",FACE,{"derivedFrom":[makeQuery(id+"F3.opExtrude","SWEPT_FACE",FACE,{"disambiguationData":[OSD([subQ1,subQ0])]}),makeQuery(id+"F5.opExtrude","SWEPT_FACE",FACE,{"disambiguationData":[OSD([sQuery(id+"F4.wireOp",EDGE,"E9")])]}),makeQuery(id+"F5.opExtrude","SWEPT_FACE",FACE,{"disambiguationData":[OSD([sQuery(id+"F4.wireOp",EDGE,"E11.MirrorCS")])]})]}),makeQuery(id+"F7.opExtrude","CAP_FACE",FACE,{"disambiguationData":[OSD([sQuery(id+"F6.wireOp",EDGE,"E16"),sQuery(id+"F6.wireOp",EDGE,"E17")])],"isStart":true}),makeQuery(id+"F7.opExtrude","CAP_FACE",FACE,{"disambiguationData":[OSD([subQ1,subQ0,sQuery(id+"F6.wireOp",EDGE,"E18.1.0.0")])],"isStart":true}),makeQuery(id+"F7.opExtrude","CAP_FACE",FACE,{"disambiguationData":[OSD([subQ1,subQ0,sQuery(id+"F6.wireOp",EDGE,"E18.2.0.0")])],"isStart":true}),makeQuery(id+"F7.opExtrude","CAP_FACE",FACE,{"disambiguationData":[OSD([subQ1,subQ0,sQuery(id+"F6.wireOp",EDGE,"E18.3.0.0")])],"isStart":true}),makeQuery(id+"F7.opExtrude","CAP_FACE",FACE,{"disambiguationData":[OSD([subQ1,subQ0,sQuery(id+"F6.wireOp",EDGE,"E18.4.0.0")])],"isStart":true}),makeQuery(id+"F7.opExtrude","CAP_FACE",FACE,{"disambiguationData":[OSD([subQ1,subQ0,sQuery(id+"F6.wireOp",EDGE,"E18.5.0.0")])],"isStart":true}),makeQuery(id+"F7.opExtrude","CAP_FACE",FACE,{"disambiguationData":[OSD([subQ1,subQ0,sQuery(id+"F6.wireOp",EDGE,"E18.6.0.0")])],"isStart":true}),makeQuery(id+"F7.opExtrude","CAP_FACE",FACE,{"disambiguationData":[OSD([subQ1,subQ0,sQuery(id+"F6.wireOp",EDGE,"E18.7.0.0")])],"isStart":true}),makeQuery(id+"F7.opExtrude","CAP_FACE",FACE,{"disambiguationData":[OSD([subQ1,subQ0,sQuery(id+"F6.wireOp",EDGE,"E18.8.0.0")])],"isStart":true}),makeQuery(id+"F7.opExtrude","CAP_FACE",FACE,{"disambiguationData":[OSD([subQ1,subQ0,sQuery(id+"F6.wireOp",EDGE,"E18.9.0.0")])],"isStart":true})]}),makeQuery(id+"F31.opExtrude","SWEPT_FACE",FACE,{"disambiguationData":[OSD([sQuery(id+"F30.wireOp",EDGE,"LmbyR1he-35kO-f53Q-696j-YAIKVnODTwI9")])]}),makeQuery(id+"F31.opExtrude","SWEPT_FACE",FACE,{"disambiguationData":[OSD([sQuery(id+"F30.wireOp",EDGE,"lc0urJVt-xGFD-1UqV-AUzd-Ddt8hkDyLtwQ"),sQuery(id+"F30.wireOp",EDGE,"9e28845e-500e-4894-8802-eb7ad12137a13.MirrorCS")])]}),makeQuery(id+"F31.opExtrude","SWEPT_FACE",FACE,{"disambiguationData":[OSD([sQuery(id+"F30.wireOp",EDGE,"9e28845e-500e-4894-8802-eb7ad12137a10.MirrorCS")])]})]})]});}
            var Q14;
            Q14=makeQuery(id+"F31.boolean.opBoolean","MERGE",EDGE,{"derivedFrom":[makeQuery(id+"F5.boolean.opBoolean","MERGE",EDGE,{"derivedFrom":[makeQuery(id+"F3.opExtrude","SWEPT_EDGE",EDGE,{"disambiguationData":[OSD([sQuery(id+"F2.wireOp",EDGE,"E4.MirrorCS"),sQuery(id+"F2.wireOp",EDGE,"E5.MirrorCS")])]}),makeQuery(id+"F5.opExtrude","SWEPT_EDGE",EDGE,{"disambiguationData":[OSD([sQuery(id+"F4.wireOp",EDGE,"E11.MirrorCS"),sQuery(id+"F4.wireOp",EDGE,"E12.MirrorCS")])]})]}),makeQuery(id+"F31.opExtrude","SWEPT_EDGE",EDGE,{"disambiguationData":[OSD([sQuery(id+"F30.wireOp",EDGE,"9e28845e-500e-4894-8802-eb7ad12137a10.MirrorCS"),sQuery(id+"F30.wireOp",EDGE,"E78.MirrorCS")])]})]});
            var Q15;
            Q15=makeQuery(id+"F5.opExtrude","CAP_EDGE",EDGE,{"disambiguationData":[OSD([sQuery(id+"F4.wireOp",EDGE,"E11.MirrorCS")])],"isStart":false});
            var Q16;
            Q16=makeQuery(id+"F5.opExtrude","SWEPT_EDGE",EDGE,{"disambiguationData":[OSD([sQuery(id+"F2.wireOp",EDGE,"E2"),sQuery(id+"F2.wireOp",EDGE,"E5.MirrorCS"),sQuery(id+"F4.wireOp",EDGE,"E10.MirrorCS"),sQuery(id+"F4.wireOp",EDGE,"E11.MirrorCS")])]});
            var Q17;
            Q17=makeQuery(id+"F5.opExtrude","CAP_EDGE",EDGE,{"disambiguationData":[OSD([sQuery(id+"F4.wireOp",EDGE,"E12.MirrorCS")])],"isStart":false});
            var Q18;
            Q18=makeQuery(id+"F5.opExtrude","CAP_EDGE",EDGE,{"disambiguationData":[OSD([sQuery(id+"F4.wireOp",EDGE,"E10.MirrorCS")])],"isStart":false});
            var Q19;
            Q19=makeQuery(id+"F5.opExtrude","CAP_EDGE",EDGE,{"disambiguationData":[OSD([sQuery(id+"F4.wireOp",EDGE,"E14")])],"isStart":false});
            var Q20;
            Q20=makeQuery(id+"F5.opExtrude","CAP_EDGE",EDGE,{"disambiguationData":[OSD([sQuery(id+"F4.wireOp",EDGE,"E8")])],"isStart":false});
            var Q21;
            {var subQ0=sQuery(id+"F2.wireOp",EDGE,"E3.MirrorCS");var subQ1=sQuery(id+"F2.wireOp",EDGE,"E0");var subQ2=sQuery(id+"F2.wireOp",EDGE,"E4.MirrorCS");Q21=makeQuery(id+"F13.boolean.opBoolean","SPLIT",EDGE,{"disambiguationData":[TD([makeQuery(id+"F3.opExtrude","SWEPT_FACE",FACE,{"disambiguationData":[OSD([subQ2])]})])],"derivedFrom":makeQuery(id+"F3.opExtrude","CAP_EDGE",EDGE,{"disambiguationData":[OSD([subQ1,subQ0])],"isStart":true})});}
            var Q22;
            {var subQ0=sQuery(id+"F2.wireOp",EDGE,"E1");var subQ1=sQuery(id+"F2.wireOp",EDGE,"E3.MirrorCS");var subQ2=sQuery(id+"F2.wireOp",EDGE,"E0");Q22=makeQuery(id+"F13.boolean.opBoolean","SPLIT",EDGE,{"disambiguationData":[TD([makeQuery(id+"F3.opExtrude","SWEPT_FACE",FACE,{"disambiguationData":[OSD([subQ0])]})])],"derivedFrom":makeQuery(id+"F3.opExtrude","CAP_EDGE",EDGE,{"disambiguationData":[OSD([subQ2,subQ1])],"isStart":true})});}
            var Q23;
            Q23=makeQuery(id+"F25.boolean.opBoolean","INTERSECT",EDGE,{"derivedFrom":[makeQuery(id+"F5.opExtrude","SWEPT_FACE",FACE,{"disambiguationData":[OSD([sQuery(id+"F4.wireOp",EDGE,"E14")])]}),makeQuery(id+"F25.opExtrude","SWEPT_FACE",FACE,{"disambiguationData":[OSD([sQuery(id+"F24.wireOp",EDGE,"E60")])]})]});
            var Q24;
            {var subQ0=sQuery(id+"F2.wireOp",EDGE,"E5.MirrorCS");var subQ1=sQuery(id+"F2.wireOp",EDGE,"E2");Q24=makeQuery(id+"F34.opChamfer","BLEND_EDGE",EDGE,{"blendedFrom":[makeQuery(id+"F31.opExtrude","CAP_EDGE",EDGE,{"disambiguationData":[OSD([sQuery(id+"F30.wireOp",EDGE,"E93")])],"isStart":false}),makeQuery(id+"F31.boolean.opBoolean","MERGE",FACE,{"derivedFrom":[makeQuery(id+"F7.boolean.opBoolean","MERGE",FACE,{"derivedFrom":[makeQuery(id+"F5.boolean.opBoolean","MERGE",FACE,{"derivedFrom":[makeQuery(id+"F3.opExtrude","SWEPT_FACE",FACE,{"disambiguationData":[OSD([subQ1,subQ0])]}),makeQuery(id+"F5.opExtrude","SWEPT_FACE",FACE,{"disambiguationData":[OSD([sQuery(id+"F4.wireOp",EDGE,"E9")])]}),makeQuery(id+"F5.opExtrude","SWEPT_FACE",FACE,{"disambiguationData":[OSD([sQuery(id+"F4.wireOp",EDGE,"E11.MirrorCS")])]})]}),makeQuery(id+"F7.opExtrude","CAP_FACE",FACE,{"disambiguationData":[OSD([sQuery(id+"F6.wireOp",EDGE,"E16"),sQuery(id+"F6.wireOp",EDGE,"E17")])],"isStart":true}),makeQuery(id+"F7.opExtrude","CAP_FACE",FACE,{"disambiguationData":[OSD([subQ1,subQ0,sQuery(id+"F6.wireOp",EDGE,"E18.1.0.0")])],"isStart":true}),makeQuery(id+"F7.opExtrude","CAP_FACE",FACE,{"disambiguationData":[OSD([subQ1,subQ0,sQuery(id+"F6.wireOp",EDGE,"E18.2.0.0")])],"isStart":true}),makeQuery(id+"F7.opExtrude","CAP_FACE",FACE,{"disambiguationData":[OSD([subQ1,subQ0,sQuery(id+"F6.wireOp",EDGE,"E18.3.0.0")])],"isStart":true}),makeQuery(id+"F7.opExtrude","CAP_FACE",FACE,{"disambiguationData":[OSD([subQ1,subQ0,sQuery(id+"F6.wireOp",EDGE,"E18.4.0.0")])],"isStart":true}),makeQuery(id+"F7.opExtrude","CAP_FACE",FACE,{"disambiguationData":[OSD([subQ1,subQ0,sQuery(id+"F6.wireOp",EDGE,"E18.5.0.0")])],"isStart":true}),makeQuery(id+"F7.opExtrude","CAP_FACE",FACE,{"disambiguationData":[OSD([subQ1,subQ0,sQuery(id+"F6.wireOp",EDGE,"E18.6.0.0")])],"isStart":true}),makeQuery(id+"F7.opExtrude","CAP_FACE",FACE,{"disambiguationData":[OSD([subQ1,subQ0,sQuery(id+"F6.wireOp",EDGE,"E18.7.0.0")])],"isStart":true})]}),makeQuery(id+"F31.opExtrude","SWEPT_FACE",FACE,{"disambiguationData":[OSD([sQuery(id+"F30.wireOp",EDGE,"E88")])]}),makeQuery(id+"F31.opExtrude","SWEPT_FACE",FACE,{"disambiguationData":[OSD([sQuery(id+"F30.wireOp",EDGE,"E89")])]}),makeQuery(id+"F31.opExtrude","SWEPT_FACE",FACE,{"disambiguationData":[OSD([sQuery(id+"F30.wireOp",EDGE,"E90")])]}),makeQuery(id+"F31.opExtrude","SWEPT_FACE",FACE,{"disambiguationData":[OSD([sQuery(id+"F30.wireOp",EDGE,"E94")])]})]})],"blendedInto":[makeQuery(id+"F31.boolean.opBoolean","MERGE",FACE,{"derivedFrom":[makeQuery(id+"F7.boolean.opBoolean","MERGE",FACE,{"derivedFrom":[makeQuery(id+"F5.boolean.opBoolean","MERGE",FACE,{"derivedFrom":[makeQuery(id+"F3.opExtrude","SWEPT_FACE",FACE,{"disambiguationData":[OSD([subQ1,subQ0])]}),makeQuery(id+"F5.opExtrude","SWEPT_FACE",FACE,{"disambiguationData":[OSD([sQuery(id+"F4.wireOp",EDGE,"E9")])]}),makeQuery(id+"F5.opExtrude","SWEPT_FACE",FACE,{"disambiguationData":[OSD([sQuery(id+"F4.wireOp",EDGE,"E11.MirrorCS")])]})]}),makeQuery(id+"F7.opExtrude","CAP_FACE",FACE,{"disambiguationData":[OSD([sQuery(id+"F6.wireOp",EDGE,"E16"),sQuery(id+"F6.wireOp",EDGE,"E17")])],"isStart":true}),makeQuery(id+"F7.opExtrude","CAP_FACE",FACE,{"disambiguationData":[OSD([subQ1,subQ0,sQuery(id+"F6.wireOp",EDGE,"E18.1.0.0")])],"isStart":true}),makeQuery(id+"F7.opExtrude","CAP_FACE",FACE,{"disambiguationData":[OSD([subQ1,subQ0,sQuery(id+"F6.wireOp",EDGE,"E18.2.0.0")])],"isStart":true}),makeQuery(id+"F7.opExtrude","CAP_FACE",FACE,{"disambiguationData":[OSD([subQ1,subQ0,sQuery(id+"F6.wireOp",EDGE,"E18.3.0.0")])],"isStart":true}),makeQuery(id+"F7.opExtrude","CAP_FACE",FACE,{"disambiguationData":[OSD([subQ1,subQ0,sQuery(id+"F6.wireOp",EDGE,"E18.4.0.0")])],"isStart":true}),makeQuery(id+"F7.opExtrude","CAP_FACE",FACE,{"disambiguationData":[OSD([subQ1,subQ0,sQuery(id+"F6.wireOp",EDGE,"E18.5.0.0")])],"isStart":true}),makeQuery(id+"F7.opExtrude","CAP_FACE",FACE,{"disambiguationData":[OSD([subQ1,subQ0,sQuery(id+"F6.wireOp",EDGE,"E18.6.0.0")])],"isStart":true}),makeQuery(id+"F7.opExtrude","CAP_FACE",FACE,{"disambiguationData":[OSD([subQ1,subQ0,sQuery(id+"F6.wireOp",EDGE,"E18.7.0.0")])],"isStart":true})]}),makeQuery(id+"F31.opExtrude","SWEPT_FACE",FACE,{"disambiguationData":[OSD([sQuery(id+"F30.wireOp",EDGE,"E88")])]}),makeQuery(id+"F31.opExtrude","SWEPT_FACE",FACE,{"disambiguationData":[OSD([sQuery(id+"F30.wireOp",EDGE,"E89")])]}),makeQuery(id+"F31.opExtrude","SWEPT_FACE",FACE,{"disambiguationData":[OSD([sQuery(id+"F30.wireOp",EDGE,"E90")])]}),makeQuery(id+"F31.opExtrude","SWEPT_FACE",FACE,{"disambiguationData":[OSD([sQuery(id+"F30.wireOp",EDGE,"E94")])]})]})]});}
            var Q25;
            {var subQ0=sQuery(id+"F2.wireOp",EDGE,"E5.MirrorCS");var subQ1=sQuery(id+"F2.wireOp",EDGE,"E2");Q25=makeQuery(id+"F31.boolean.opBoolean","SPLIT",EDGE,{"disambiguationData":[TD([makeQuery(id+"F31.opExtrude","SWEPT_FACE",FACE,{"disambiguationData":[OSD([sQuery(id+"F30.wireOp",EDGE,"E91")])]})])],"derivedFrom":makeQuery(id+"F3.opExtrude","CAP_EDGE",EDGE,{"disambiguationData":[OSD([subQ1,subQ0])],"isStart":true})});}
            var Q26;
            {var subQ0=sQuery(id+"F2.wireOp",EDGE,"E5.MirrorCS");var subQ1=sQuery(id+"F2.wireOp",EDGE,"E2");Q26=makeQuery(id+"F34.opChamfer","BLEND_EDGE",EDGE,{"blendedFrom":[makeQuery(id+"F31.opExtrude","CAP_EDGE",EDGE,{"disambiguationData":[OSD([sQuery(id+"F30.wireOp",EDGE,"E91")])],"isStart":false}),makeQuery(id+"F31.boolean.opBoolean","MERGE",FACE,{"derivedFrom":[makeQuery(id+"F7.boolean.opBoolean","MERGE",FACE,{"derivedFrom":[makeQuery(id+"F5.boolean.opBoolean","MERGE",FACE,{"derivedFrom":[makeQuery(id+"F3.opExtrude","SWEPT_FACE",FACE,{"disambiguationData":[OSD([subQ1,subQ0])]}),makeQuery(id+"F5.opExtrude","SWEPT_FACE",FACE,{"disambiguationData":[OSD([sQuery(id+"F4.wireOp",EDGE,"E9")])]}),makeQuery(id+"F5.opExtrude","SWEPT_FACE",FACE,{"disambiguationData":[OSD([sQuery(id+"F4.wireOp",EDGE,"E11.MirrorCS")])]})]}),makeQuery(id+"F7.opExtrude","CAP_FACE",FACE,{"disambiguationData":[OSD([sQuery(id+"F6.wireOp",EDGE,"E16"),sQuery(id+"F6.wireOp",EDGE,"E17")])],"isStart":true}),makeQuery(id+"F7.opExtrude","CAP_FACE",FACE,{"disambiguationData":[OSD([subQ1,subQ0,sQuery(id+"F6.wireOp",EDGE,"E18.1.0.0")])],"isStart":true}),makeQuery(id+"F7.opExtrude","CAP_FACE",FACE,{"disambiguationData":[OSD([subQ1,subQ0,sQuery(id+"F6.wireOp",EDGE,"E18.2.0.0")])],"isStart":true}),makeQuery(id+"F7.opExtrude","CAP_FACE",FACE,{"disambiguationData":[OSD([subQ1,subQ0,sQuery(id+"F6.wireOp",EDGE,"E18.3.0.0")])],"isStart":true}),makeQuery(id+"F7.opExtrude","CAP_FACE",FACE,{"disambiguationData":[OSD([subQ1,subQ0,sQuery(id+"F6.wireOp",EDGE,"E18.4.0.0")])],"isStart":true}),makeQuery(id+"F7.opExtrude","CAP_FACE",FACE,{"disambiguationData":[OSD([subQ1,subQ0,sQuery(id+"F6.wireOp",EDGE,"E18.5.0.0")])],"isStart":true}),makeQuery(id+"F7.opExtrude","CAP_FACE",FACE,{"disambiguationData":[OSD([subQ1,subQ0,sQuery(id+"F6.wireOp",EDGE,"E18.6.0.0")])],"isStart":true}),makeQuery(id+"F7.opExtrude","CAP_FACE",FACE,{"disambiguationData":[OSD([subQ1,subQ0,sQuery(id+"F6.wireOp",EDGE,"E18.7.0.0")])],"isStart":true})]}),makeQuery(id+"F31.opExtrude","SWEPT_FACE",FACE,{"disambiguationData":[OSD([sQuery(id+"F30.wireOp",EDGE,"E88")])]}),makeQuery(id+"F31.opExtrude","SWEPT_FACE",FACE,{"disambiguationData":[OSD([sQuery(id+"F30.wireOp",EDGE,"E89")])]}),makeQuery(id+"F31.opExtrude","SWEPT_FACE",FACE,{"disambiguationData":[OSD([sQuery(id+"F30.wireOp",EDGE,"E90")])]}),makeQuery(id+"F31.opExtrude","SWEPT_FACE",FACE,{"disambiguationData":[OSD([sQuery(id+"F30.wireOp",EDGE,"E94")])]})]})],"blendedInto":[makeQuery(id+"F31.boolean.opBoolean","MERGE",FACE,{"derivedFrom":[makeQuery(id+"F7.boolean.opBoolean","MERGE",FACE,{"derivedFrom":[makeQuery(id+"F5.boolean.opBoolean","MERGE",FACE,{"derivedFrom":[makeQuery(id+"F3.opExtrude","SWEPT_FACE",FACE,{"disambiguationData":[OSD([subQ1,subQ0])]}),makeQuery(id+"F5.opExtrude","SWEPT_FACE",FACE,{"disambiguationData":[OSD([sQuery(id+"F4.wireOp",EDGE,"E9")])]}),makeQuery(id+"F5.opExtrude","SWEPT_FACE",FACE,{"disambiguationData":[OSD([sQuery(id+"F4.wireOp",EDGE,"E11.MirrorCS")])]})]}),makeQuery(id+"F7.opExtrude","CAP_FACE",FACE,{"disambiguationData":[OSD([sQuery(id+"F6.wireOp",EDGE,"E16"),sQuery(id+"F6.wireOp",EDGE,"E17")])],"isStart":true}),makeQuery(id+"F7.opExtrude","CAP_FACE",FACE,{"disambiguationData":[OSD([subQ1,subQ0,sQuery(id+"F6.wireOp",EDGE,"E18.1.0.0")])],"isStart":true}),makeQuery(id+"F7.opExtrude","CAP_FACE",FACE,{"disambiguationData":[OSD([subQ1,subQ0,sQuery(id+"F6.wireOp",EDGE,"E18.2.0.0")])],"isStart":true}),makeQuery(id+"F7.opExtrude","CAP_FACE",FACE,{"disambiguationData":[OSD([subQ1,subQ0,sQuery(id+"F6.wireOp",EDGE,"E18.3.0.0")])],"isStart":true}),makeQuery(id+"F7.opExtrude","CAP_FACE",FACE,{"disambiguationData":[OSD([subQ1,subQ0,sQuery(id+"F6.wireOp",EDGE,"E18.4.0.0")])],"isStart":true}),makeQuery(id+"F7.opExtrude","CAP_FACE",FACE,{"disambiguationData":[OSD([subQ1,subQ0,sQuery(id+"F6.wireOp",EDGE,"E18.5.0.0")])],"isStart":true}),makeQuery(id+"F7.opExtrude","CAP_FACE",FACE,{"disambiguationData":[OSD([subQ1,subQ0,sQuery(id+"F6.wireOp",EDGE,"E18.6.0.0")])],"isStart":true}),makeQuery(id+"F7.opExtrude","CAP_FACE",FACE,{"disambiguationData":[OSD([subQ1,subQ0,sQuery(id+"F6.wireOp",EDGE,"E18.7.0.0")])],"isStart":true})]}),makeQuery(id+"F31.opExtrude","SWEPT_FACE",FACE,{"disambiguationData":[OSD([sQuery(id+"F30.wireOp",EDGE,"E88")])]}),makeQuery(id+"F31.opExtrude","SWEPT_FACE",FACE,{"disambiguationData":[OSD([sQuery(id+"F30.wireOp",EDGE,"E89")])]}),makeQuery(id+"F31.opExtrude","SWEPT_FACE",FACE,{"disambiguationData":[OSD([sQuery(id+"F30.wireOp",EDGE,"E90")])]}),makeQuery(id+"F31.opExtrude","SWEPT_FACE",FACE,{"disambiguationData":[OSD([sQuery(id+"F30.wireOp",EDGE,"E94")])]})]})]});}
            var Q27;
            Q27=makeQuery(id+"F31.opExtrude","CAP_EDGE",EDGE,{"disambiguationData":[OSD([sQuery(id+"F30.wireOp",EDGE,"E90")])],"isStart":false});
            var Q28;
            Q28=makeQuery(id+"F31.opExtrude","CAP_EDGE",EDGE,{"disambiguationData":[OSD([sQuery(id+"F30.wireOp",EDGE,"E94")])],"isStart":false});
            chamfer(context, id + "F36", {"entities" : qUnion([Q0, Q1, Q2, Q3, Q4, Q5, Q6, Q7, Q8, Q9, Q10, Q11, Q12, Q13, Q14, Q15, Q16, Q17, Q18, Q19, Q20, Q21, Q22, Q23, Q24, Q25, Q26, Q27, Q28]), "width" : 1 * mm, "tangentPropagation" : true});
        }
        {
            var Q0;
            Q0=makeQuery(id+"F5.opExtrude","SWEPT_EDGE",EDGE,{"disambiguationData":[OSD([sQuery(id+"F4.wireOp",EDGE,"E8"),sQuery(id+"F4.wireOp",EDGE,"E14")])]});
            var Q1;
            Q1=makeQuery(id+"F5.opExtrude","SWEPT_EDGE",EDGE,{"disambiguationData":[OSD([sQuery(id+"F4.wireOp",EDGE,"E10.MirrorCS"),sQuery(id+"F4.wireOp",EDGE,"E14")])]});
            fillet(context, id + "F37", {"entities" : qUnion([Q0, Q1]), "radius" : 5 * mm, "tangentPropagation" : true, "allowEdgeOverflow" : false});
        }
    });
